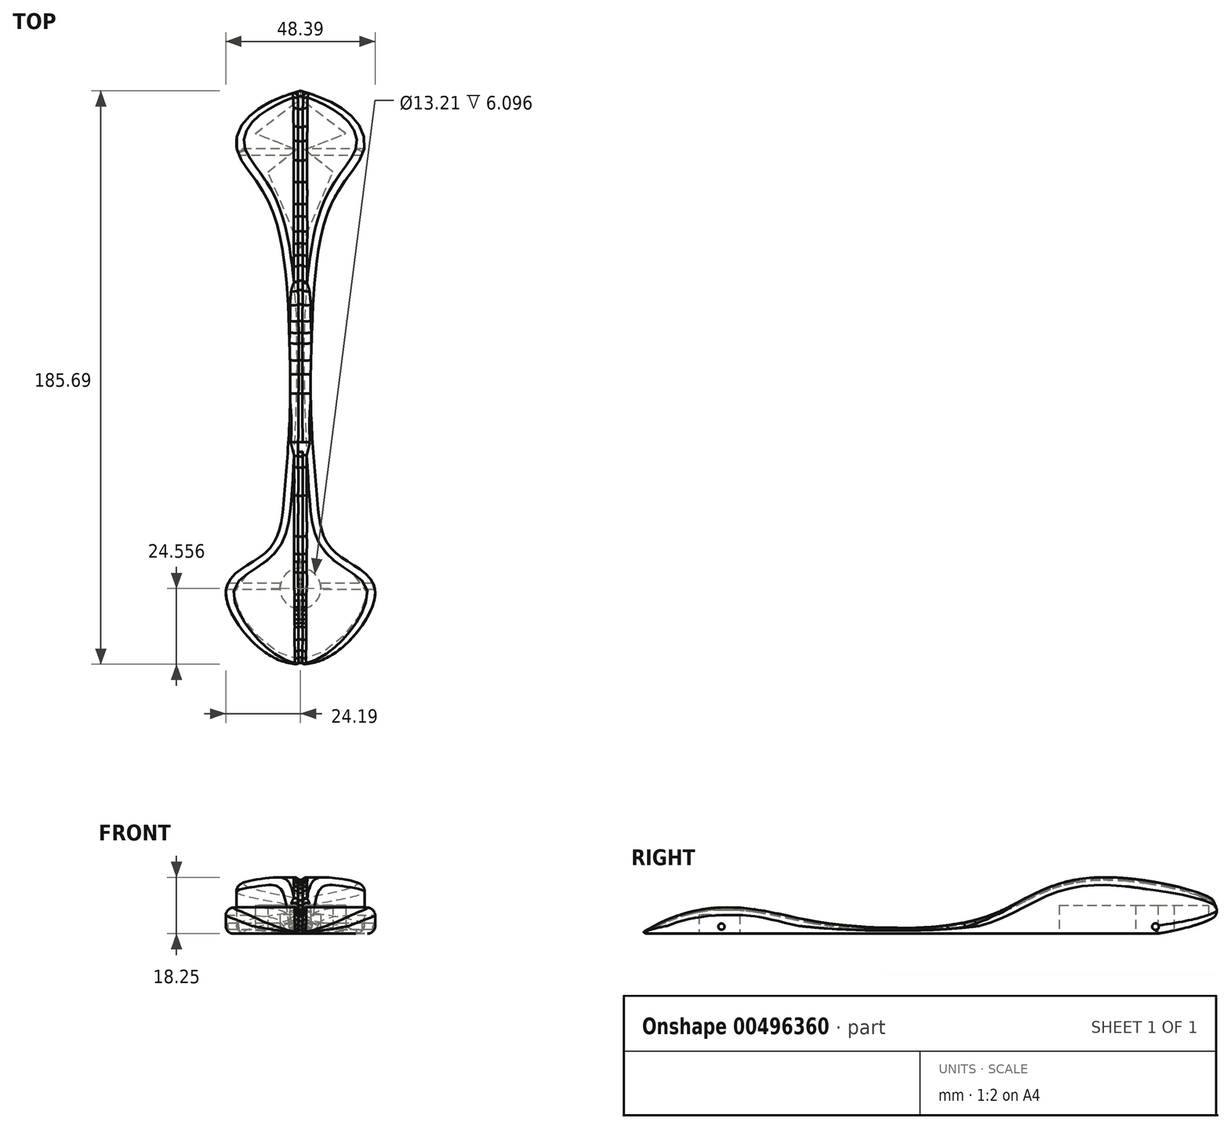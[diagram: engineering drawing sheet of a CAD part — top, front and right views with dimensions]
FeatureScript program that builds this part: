
annotation { "Feature Type Name" : "Feature", "Feature Type Description" : "" }
export const myFeature = defineFeature(function(context is Context, id is Id, definition is map)
    precondition{}
    {
        {
            var Q0;
            Q0=qCreatedBy(makeId("Right.planeOp"),FACE);
            var sketch = newSketch(context, id + "F0", { "sketchPlane" : qUnion([Q0])});
            skLineSegment(sketch, "E0", {"start": v(-99.64, 0) * mm, "end": v(67.86, 0) * mm});
            skFitSpline(sketch, "E1", {"points": [v(-99.64, 0) * mm, v(-58.26, 7.1) * mm, v(-36.9, 3.05) * mm, v(13.17, 6.08) * mm, v(63.97, 17.2) * mm, v(67.86, 0) * mm], "startDerivative": vector(226.28, 146.37) * mm, "endDerivative": vector(-818.18, -147.8) * mm});
            skCircle(sketch, "E2", {"center": v(-73.57, 2.29) * mm, "radius": 1.02 * mm});
            skCircle(sketch, "E3", {"center": v(67.09, 2.29) * mm, "radius": 1.08 * mm});
            skSolve(sketch);
        }
        {
            var Q0;
            Q0=makeQuery(id+"F0.imprint","IMPRINT",FACE,{"disambiguationData":[TD([[makeQuery(id+"F0.imprint","IMPRINT",EDGE,{"derivedFrom":sQuery(id+"F0.wireOp",EDGE,"E0")}),1.0]])]});
            extrude(context, id + "F1", {"entities" : qUnion([Q0]), "depth" : 81.28 * mm, "symmetric" : true});
        }
        {
            var Q0;
            Q0=qCreatedBy(makeId("Top.planeOp"),FACE);
            var sketch = newSketch(context, id + "F2", { "sketchPlane" : qUnion([Q0])});
            skFitSpline(sketch, "E4", {"points": [v(0.02, 86.91) * mm, v(-20.51, 67.7) * mm, v(-8.81, 47.48) * mm, v(-5.03, -39.8) * mm, v(-11.33, -62.63) * mm, v(-24.17, -75.03) * mm, v(0, -99.95) * mm], "startDerivative": vector(-340.64, -92.8) * mm, "endDerivative": vector(192.17, -7.55) * mm});
            skLineSegment(sketch, "E5", {"start": v(0.02, 86.91) * mm, "end": v(0.02, 86.91) * mm});
            skLineSegment(sketch, "E6.bottom", {"start": v(-52.6, 103.82) * mm, "end": v(52.64, 103.82) * mm});
            skLineSegment(sketch, "E6.top", {"start": v(-52.6, -103.34) * mm, "end": v(52.64, -103.34) * mm});
            skLineSegment(sketch, "E6.left", {"start": v(-52.6, 103.82) * mm, "end": v(-52.6, -103.34) * mm});
            skLineSegment(sketch, "E6.right", {"start": v(52.64, 103.82) * mm, "end": v(52.64, -103.34) * mm});
            skPoint(sketch, "E7.endSnap0", {"position": v(0.02, -103.34) * mm});
            skFitSpline(sketch, "E8.MirrorCS", {"points": [v(0.02, 86.91) * mm, v(20.55, 67.7) * mm, v(8.85, 47.48) * mm, v(5.05, -39.8) * mm, v(11.34, -62.63) * mm, v(24.17, -75.04) * mm, v(0, -99.95) * mm], "startDerivative": vector(340.62, -92.88) * mm, "endDerivative": vector(-192.17, -7.51) * mm});
            skSolve(sketch);
        }
        {
            var Q0;
            Q0=makeQuery(id+"F2.imprint","IMPRINT",FACE,{"disambiguationData":[TD([[makeQuery(id+"F2.imprint","IMPRINT",EDGE,{"derivedFrom":sQuery(id+"F2.wireOp",EDGE,"E6.top")}),1.0]])]});
            var Q1;
            Q1=qNothing();
            var Q2;
            Q2=qNothing();
            extrude(context, id + "F3", {"entities" : qUnion([Q0, Q1, Q2]), "operationType" : NewBodyOperationType.REMOVE, "oppositeDirection" : true, "depth" : 71.37 * mm, "offsetDistance" : 25.4 * mm, "symmetric" : true});
        }
        {
            var Q0;
            Q0=makeQuery(id+"F3.boolean.opBoolean","INTERSECT",EDGE,{"disambiguationData":[OD(1.0)],"derivedFrom":[makeQuery(id+"F1.opExtrude","SWEPT_FACE",FACE,{"disambiguationData":[OSD([sQuery(id+"F0.wireOp",EDGE,"E1")])]}),makeQuery(id+"F3.opExtrude","SWEPT_FACE",FACE,{"disambiguationData":[OSD([sQuery(id+"F2.wireOp",EDGE,"E8.MirrorCS")])]})]});
            var Q1;
            Q1=makeQuery(id+"F3.boolean.opBoolean","INTERSECT",EDGE,{"derivedFrom":[makeQuery(id+"F1.opExtrude","SWEPT_FACE",FACE,{"disambiguationData":[OSD([sQuery(id+"F0.wireOp",EDGE,"E0")])]}),makeQuery(id+"F3.opExtrude","SWEPT_FACE",FACE,{"disambiguationData":[OSD([sQuery(id+"F2.wireOp",EDGE,"E8.MirrorCS")])]})]});
            var Q2;
            Q2=makeQuery(id+"F3.boolean.opBoolean","INTERSECT",EDGE,{"derivedFrom":[makeQuery(id+"F1.opExtrude","SWEPT_FACE",FACE,{"disambiguationData":[OSD([sQuery(id+"F0.wireOp",EDGE,"E0")])]}),makeQuery(id+"F3.opExtrude","SWEPT_FACE",FACE,{"disambiguationData":[OSD([sQuery(id+"F2.wireOp",EDGE,"E4")])]})]});
            var Q3;
            Q3=makeQuery(id+"F3.boolean.opBoolean","INTERSECT",EDGE,{"disambiguationData":[OD(1.0)],"derivedFrom":[makeQuery(id+"F1.opExtrude","SWEPT_FACE",FACE,{"disambiguationData":[OSD([sQuery(id+"F0.wireOp",EDGE,"E1")])]}),makeQuery(id+"F3.opExtrude","SWEPT_FACE",FACE,{"disambiguationData":[OSD([sQuery(id+"F2.wireOp",EDGE,"E4")])]})]});
            var Q4;
            Q4=makeQuery(id+"F3.boolean.opBoolean","INTERSECT",EDGE,{"disambiguationData":[OD(0.0)],"derivedFrom":[makeQuery(id+"F1.opExtrude","SWEPT_FACE",FACE,{"disambiguationData":[OSD([sQuery(id+"F0.wireOp",EDGE,"E1")])]}),makeQuery(id+"F3.opExtrude","SWEPT_FACE",FACE,{"disambiguationData":[OSD([sQuery(id+"F2.wireOp",EDGE,"E4")])]})]});
            var Q5;
            Q5=makeQuery(id+"F3.boolean.opBoolean","INTERSECT",EDGE,{"disambiguationData":[OD(0.0)],"derivedFrom":[makeQuery(id+"F1.opExtrude","SWEPT_FACE",FACE,{"disambiguationData":[OSD([sQuery(id+"F0.wireOp",EDGE,"E1")])]}),makeQuery(id+"F3.opExtrude","SWEPT_FACE",FACE,{"disambiguationData":[OSD([sQuery(id+"F2.wireOp",EDGE,"E8.MirrorCS")])]})]});
            fillet(context, id + "F4", {"entities" : qUnion([Q0, Q1, Q2, Q3, Q4, Q5]), "radius" : 2.5 * mm, "tangentPropagation" : true, "allowEdgeOverflow" : false});
        }
        {
            var Q0;
            {var subQ0=sQuery(id+"F0.wireOp",EDGE,"E1");var subQ1=sQuery(id+"F0.wireOp",EDGE,"E0");Q0=makeQuery(id+"F1.opExtrude","SWEPT_EDGE",EDGE,{"disambiguationData":[OSD([subQ1,subQ0]),TDD([makeQuery(id+"F0.imprint","INTERSECT",VERTEX,{"disambiguationData":[OD(1.0)],"derivedFrom":[subQ1,subQ0]})])]});}
            fillet(context, id + "F5", {"entities" : qUnion([Q0]), "radius" : 2.5 * mm, "tangentPropagation" : true, "allowEdgeOverflow" : false});
        }
        {
            var Q0;
            Q0=qCreatedBy(makeId("Right.planeOp"),FACE);
            var sketch = newSketch(context, id + "F6", { "sketchPlane" : qUnion([Q0])});
            skLineSegment(sketch, "E9", {"start": v(-100.12, -0.3) * mm, "end": v(-96.89, 1.73) * mm});
            skLineSegment(sketch, "E10", {"start": v(-96.89, 1.73) * mm, "end": v(-94.53, 3) * mm});
            skLineSegment(sketch, "E11", {"start": v(-94.53, 3) * mm, "end": v(-90.9, 4.62) * mm});
            skLineSegment(sketch, "E12", {"start": v(-90.9, 4.62) * mm, "end": v(-86.85, 6.14) * mm});
            skLineSegment(sketch, "E13", {"start": v(-86.85, 6.14) * mm, "end": v(-85.54, 6.53) * mm});
            skLineSegment(sketch, "E14", {"start": v(-85.54, 6.53) * mm, "end": v(-84.06, 6.9) * mm});
            skLineSegment(sketch, "E15", {"start": v(-84.06, 6.9) * mm, "end": v(-82.72, 7.27) * mm});
            skLineSegment(sketch, "E16", {"start": v(-82.72, 7.27) * mm, "end": v(-81.34, 7.55) * mm});
            skLineSegment(sketch, "E17", {"start": v(-81.34, 7.55) * mm, "end": v(-80.05, 7.77) * mm});
            skLineSegment(sketch, "E18", {"start": v(-80.05, 7.77) * mm, "end": v(-78.2, 8.05) * mm});
            skLineSegment(sketch, "E19", {"start": v(-78.2, 8.05) * mm, "end": v(-76.17, 8.31) * mm});
            skLineSegment(sketch, "E20", {"start": v(-76.17, 8.31) * mm, "end": v(-75.14, 8.31) * mm});
            skLineSegment(sketch, "E21", {"start": v(-75.14, 8.31) * mm, "end": v(-74.38, 8.31) * mm});
            skLineSegment(sketch, "E22", {"start": v(-74.38, 8.31) * mm, "end": v(-73.62, 8.31) * mm});
            skLineSegment(sketch, "E23", {"start": v(-73.62, 8.31) * mm, "end": v(-72.47, 8.31) * mm});
            skLineSegment(sketch, "E24", {"start": v(-72.47, 8.31) * mm, "end": v(-70.97, 8.31) * mm});
            skLineSegment(sketch, "E25", {"start": v(-70.97, 8.31) * mm, "end": v(-69.08, 8.31) * mm});
            skLineSegment(sketch, "E26", {"start": v(-69.08, 8.31) * mm, "end": v(-65.6, 8.05) * mm});
            skLineSegment(sketch, "E27", {"start": v(-65.6, 8.05) * mm, "end": v(-63.1, 7.77) * mm});
            skLineSegment(sketch, "E28", {"start": v(-63.1, 7.77) * mm, "end": v(-61.86, 7.55) * mm});
            skLineSegment(sketch, "E29", {"start": v(-61.86, 7.55) * mm, "end": v(-57.31, 6.74) * mm});
            skLineSegment(sketch, "E30", {"start": v(-57.31, 6.74) * mm, "end": v(-50.98, 5.38) * mm});
            skLineSegment(sketch, "E31", {"start": v(-50.98, 5.38) * mm, "end": v(-44.16, 3.93) * mm});
            skLineSegment(sketch, "E32", {"start": v(-44.16, 3.93) * mm, "end": v(-39.73, 3.3) * mm});
            skLineSegment(sketch, "E33", {"start": v(-39.73, 3.3) * mm, "end": v(-35.03, 2.65) * mm});
            skLineSegment(sketch, "E34", {"start": v(-35.03, 2.65) * mm, "end": v(-31.08, 2.3) * mm});
            skLineSegment(sketch, "E35", {"start": v(-31.08, 2.3) * mm, "end": v(-29.62, 2.18) * mm});
            skLineSegment(sketch, "E36", {"start": v(-29.62, 2.18) * mm, "end": v(-26.88, 1.95) * mm});
            skLineSegment(sketch, "E37", {"start": v(-26.88, 1.95) * mm, "end": v(-11.11, 1.95) * mm});
            skLineSegment(sketch, "E38", {"start": v(-11.11, 1.95) * mm, "end": v(-4.94, 2.3) * mm});
            skLineSegment(sketch, "E39", {"start": v(-4.94, 2.3) * mm, "end": v(-0.44, 2.85) * mm});
            skLineSegment(sketch, "E40", {"start": v(-0.44, 2.85) * mm, "end": v(5.05, 3.71) * mm});
            skLineSegment(sketch, "E41", {"start": v(5.05, 3.71) * mm, "end": v(8.48, 4.5) * mm});
            skLineSegment(sketch, "E42", {"start": v(8.48, 4.5) * mm, "end": v(12.27, 5.6) * mm});
            skLineSegment(sketch, "E43", {"start": v(12.27, 5.6) * mm, "end": v(17.56, 7.55) * mm});
            skLineSegment(sketch, "E44", {"start": v(17.56, 7.55) * mm, "end": v(22.11, 9.75) * mm});
            skLineSegment(sketch, "E45", {"start": v(22.11, 9.75) * mm, "end": v(25.16, 11.37) * mm});
            skLineSegment(sketch, "E46", {"start": v(25.16, 11.37) * mm, "end": v(30.14, 13.72) * mm});
            skLineSegment(sketch, "E47", {"start": v(30.14, 13.72) * mm, "end": v(33.58, 15.2) * mm});
            skLineSegment(sketch, "E48", {"start": v(33.58, 15.2) * mm, "end": v(37.43, 16.39) * mm});
            skLineSegment(sketch, "E49", {"start": v(37.43, 16.39) * mm, "end": v(41.38, 17.17) * mm});
            skLineSegment(sketch, "E50", {"start": v(41.38, 17.17) * mm, "end": v(46.2, 17.83) * mm});
            skLineSegment(sketch, "E51", {"start": v(46.2, 17.83) * mm, "end": v(50.27, 18.01) * mm});
            skLineSegment(sketch, "E52", {"start": v(50.27, 18.01) * mm, "end": v(57.35, 17.73) * mm});
            skLineSegment(sketch, "E53", {"start": v(57.35, 17.73) * mm, "end": v(64.38, 16.89) * mm});
            skLineSegment(sketch, "E54", {"start": v(64.38, 16.89) * mm, "end": v(70.72, 15.74) * mm});
            skLineSegment(sketch, "E55", {"start": v(70.72, 15.74) * mm, "end": v(75.31, 14.6) * mm});
            skLineSegment(sketch, "E56", {"start": v(75.31, 14.6) * mm, "end": v(81.23, 12.8) * mm});
            skLineSegment(sketch, "E57", {"start": v(81.23, 12.8) * mm, "end": v(85.48, 10.83) * mm});
            skLineSegment(sketch, "E58", {"start": v(85.48, 10.83) * mm, "end": v(90.33, 4.3) * mm});
            skSolve(sketch);
        }
        {
            var Q0;
            Q0=qCreatedBy(makeId("Front.planeOp"),FACE);
            var Q1;
            Q1=sQuery(id+"F6.wireOp",VERTEX,"E9.start");
            cPlane(context, id + "F7", {"entities" : qUnion([Q0, Q1]), "cplaneType" : CPlaneType.PLANE_POINT, "offset" : 91.95 * mm, "width" : 152.4 * mm, "height" : 152.4 * mm});
        }
        {
            var Q0;
            Q0=qCreatedBy(id+"F7.planeOp",FACE);
            var sketch = newSketch(context, id + "F8", { "sketchPlane" : qUnion([Q0])});
            skCircle(sketch, "E59", {"center": v(0, 0) * mm, "radius": 1 * mm});
            skSolve(sketch);
        }
        {
            var Q0;
            Q0=makeQuery(id+"F8.imprint","IMPRINT",FACE,{"disambiguationData":[TD([[makeQuery(id+"F8.imprint","IMPRINT",EDGE,{"derivedFrom":sQuery(id+"F8.wireOp",EDGE,"E59")}),1.0]])]});
            var Q1;
            Q1=sQuery(id+"F6.wireOp",EDGE,"E9");
            var Q2;
            Q2=sQuery(id+"F6.wireOp",EDGE,"E10");
            var Q3;
            Q3=sQuery(id+"F6.wireOp",EDGE,"E37");
            var Q4;
            Q4=sQuery(id+"F6.wireOp",EDGE,"E58");
            var Q5;
            Q5=sQuery(id+"F6.wireOp",EDGE,"E11");
            var Q6;
            Q6=sQuery(id+"F6.wireOp",EDGE,"E12");
            var Q7;
            Q7=sQuery(id+"F6.wireOp",EDGE,"E18");
            var Q8;
            Q8=sQuery(id+"F6.wireOp",EDGE,"E49");
            var Q9;
            Q9=sQuery(id+"F6.wireOp",EDGE,"E43");
            var Q10;
            Q10=sQuery(id+"F6.wireOp",EDGE,"E27");
            var Q11;
            Q11=sQuery(id+"F6.wireOp",EDGE,"E50");
            var Q12;
            Q12=sQuery(id+"F6.wireOp",EDGE,"E34");
            var Q13;
            Q13=sQuery(id+"F6.wireOp",EDGE,"E51");
            var Q14;
            Q14=sQuery(id+"F6.wireOp",EDGE,"E44");
            var Q15;
            Q15=sQuery(id+"F6.wireOp",EDGE,"E28");
            var Q16;
            Q16=sQuery(id+"F6.wireOp",EDGE,"E52");
            var Q17;
            Q17=sQuery(id+"F6.wireOp",EDGE,"E36");
            var Q18;
            Q18=sQuery(id+"F6.wireOp",EDGE,"E54");
            var Q19;
            Q19=sQuery(id+"F6.wireOp",EDGE,"E45");
            var Q20;
            Q20=sQuery(id+"F6.wireOp",EDGE,"E38");
            var Q21;
            Q21=sQuery(id+"F6.wireOp",EDGE,"E29");
            var Q22;
            Q22=sQuery(id+"F6.wireOp",EDGE,"E53");
            var Q23;
            Q23=sQuery(id+"F6.wireOp",EDGE,"E55");
            var Q24;
            Q24=sQuery(id+"F6.wireOp",EDGE,"E39");
            var Q25;
            Q25=sQuery(id+"F6.wireOp",EDGE,"E46");
            var Q26;
            Q26=sQuery(id+"F6.wireOp",EDGE,"E30");
            var Q27;
            Q27=sQuery(id+"F6.wireOp",EDGE,"E56");
            var Q28;
            Q28=sQuery(id+"F6.wireOp",EDGE,"E40");
            var Q29;
            Q29=sQuery(id+"F6.wireOp",EDGE,"E47");
            var Q30;
            Q30=sQuery(id+"F6.wireOp",EDGE,"E31");
            var Q31;
            Q31=sQuery(id+"F6.wireOp",EDGE,"E57");
            var Q32;
            Q32=sQuery(id+"F6.wireOp",EDGE,"E41");
            var Q33;
            Q33=sQuery(id+"F6.wireOp",EDGE,"E48");
            var Q34;
            Q34=sQuery(id+"F6.wireOp",EDGE,"E32");
            var Q35;
            Q35=sQuery(id+"F6.wireOp",EDGE,"E42");
            var Q36;
            Q36=sQuery(id+"F6.wireOp",EDGE,"E26");
            var Q37;
            Q37=sQuery(id+"F6.wireOp",EDGE,"E17");
            var Q38;
            Q38=sQuery(id+"F6.wireOp",EDGE,"E33");
            var Q39;
            Q39=sQuery(id+"F6.wireOp",EDGE,"E35");
            var Q40;
            Q40=sQuery(id+"F6.wireOp",EDGE,"E13");
            var Q41;
            Q41=sQuery(id+"F6.wireOp",EDGE,"E16");
            var Q42;
            Q42=sQuery(id+"F6.wireOp",EDGE,"E15");
            var Q43;
            Q43=sQuery(id+"F6.wireOp",EDGE,"E14");
            var Q44;
            Q44=sQuery(id+"F6.wireOp",EDGE,"E23");
            var Q45;
            Q45=sQuery(id+"F6.wireOp",EDGE,"E19");
            var Q46;
            Q46=sQuery(id+"F6.wireOp",EDGE,"E21");
            var Q47;
            Q47=sQuery(id+"F6.wireOp",EDGE,"E25");
            var Q48;
            Q48=sQuery(id+"F6.wireOp",EDGE,"E22");
            var Q49;
            Q49=sQuery(id+"F6.wireOp",EDGE,"E24");
            var Q50;
            Q50=sQuery(id+"F6.wireOp",EDGE,"E20");
            sweep(context, id + "F9", {"operationType" : NewBodyOperationType.REMOVE, "profiles" : qUnion([Q0]), "path" : qUnion([Q1, Q2, Q3, Q4, Q5, Q6, Q7, Q8, Q9, Q10, Q11, Q12, Q13, Q14, Q15, Q16, Q17, Q18, Q19, Q20, Q21, Q22, Q23, Q24, Q25, Q26, Q27, Q28, Q29, Q30, Q31, Q32, Q33, Q34, Q35, Q36, Q37, Q38, Q39, Q40, Q41, Q42, Q43, Q44, Q45, Q46, Q47, Q48, Q49, Q50])});
        }
        {
            var Q0;
            Q0=makeQuery(id+"F9.boolean.opBoolean","INTERSECT",EDGE,{"disambiguationData":[OD(1.0)],"derivedFrom":[makeQuery(id+"F3.boolean.opBoolean","SPLIT",FACE,{"disambiguationData":[OD(0.0)],"derivedFrom":makeQuery(id+"F1.opExtrude","SWEPT_FACE",FACE,{"disambiguationData":[OSD([sQuery(id+"F0.wireOp",EDGE,"E1")])]})}),makeQuery(id+"F9.opSweep","SWEPT_FACE",FACE,{"disambiguationData":[OSD([sQuery(id+"F6.wireOp",EDGE,"E9"),sQuery(id+"F8.wireOp",EDGE,"E59")])]})]});
            var Q1;
            Q1=makeQuery(id+"F9.boolean.opBoolean","INTERSECT",EDGE,{"disambiguationData":[OD(1.0)],"derivedFrom":[makeQuery(id+"F3.boolean.opBoolean","SPLIT",FACE,{"disambiguationData":[OD(0.0)],"derivedFrom":makeQuery(id+"F1.opExtrude","SWEPT_FACE",FACE,{"disambiguationData":[OSD([sQuery(id+"F0.wireOp",EDGE,"E1")])]})}),makeQuery(id+"F9.opSweep","SWEPT_FACE",FACE,{"disambiguationData":[OSD([sQuery(id+"F6.wireOp",EDGE,"E10"),sQuery(id+"F8.wireOp",EDGE,"E59")])]})]});
            var Q2;
            Q2=makeQuery(id+"F9.boolean.opBoolean","INTERSECT",EDGE,{"disambiguationData":[OD(1.0)],"derivedFrom":[makeQuery(id+"F3.boolean.opBoolean","SPLIT",FACE,{"disambiguationData":[OD(0.0)],"derivedFrom":makeQuery(id+"F1.opExtrude","SWEPT_FACE",FACE,{"disambiguationData":[OSD([sQuery(id+"F0.wireOp",EDGE,"E1")])]})}),makeQuery(id+"F9.opSweep","SWEPT_FACE",FACE,{"disambiguationData":[OSD([sQuery(id+"F6.wireOp",EDGE,"E11"),sQuery(id+"F8.wireOp",EDGE,"E59")])]})]});
            var Q3;
            Q3=makeQuery(id+"F9.boolean.opBoolean","INTERSECT",EDGE,{"disambiguationData":[OD(1.0)],"derivedFrom":[makeQuery(id+"F3.boolean.opBoolean","SPLIT",FACE,{"disambiguationData":[OD(0.0)],"derivedFrom":makeQuery(id+"F1.opExtrude","SWEPT_FACE",FACE,{"disambiguationData":[OSD([sQuery(id+"F0.wireOp",EDGE,"E1")])]})}),makeQuery(id+"F9.opSweep","SWEPT_FACE",FACE,{"disambiguationData":[OSD([sQuery(id+"F6.wireOp",EDGE,"E12"),sQuery(id+"F8.wireOp",EDGE,"E59")])]})]});
            var Q4;
            Q4=makeQuery(id+"F9.boolean.opBoolean","INTERSECT",EDGE,{"disambiguationData":[OD(1.0)],"derivedFrom":[makeQuery(id+"F3.boolean.opBoolean","SPLIT",FACE,{"disambiguationData":[OD(0.0)],"derivedFrom":makeQuery(id+"F1.opExtrude","SWEPT_FACE",FACE,{"disambiguationData":[OSD([sQuery(id+"F0.wireOp",EDGE,"E1")])]})}),makeQuery(id+"F9.opSweep","SWEPT_FACE",FACE,{"disambiguationData":[OSD([sQuery(id+"F6.wireOp",EDGE,"E13"),sQuery(id+"F8.wireOp",EDGE,"E59")])]})]});
            var Q5;
            Q5=makeQuery(id+"F9.boolean.opBoolean","INTERSECT",EDGE,{"disambiguationData":[OD(1.0)],"derivedFrom":[makeQuery(id+"F3.boolean.opBoolean","SPLIT",FACE,{"disambiguationData":[OD(0.0)],"derivedFrom":makeQuery(id+"F1.opExtrude","SWEPT_FACE",FACE,{"disambiguationData":[OSD([sQuery(id+"F0.wireOp",EDGE,"E1")])]})}),makeQuery(id+"F9.opSweep","SWEPT_FACE",FACE,{"disambiguationData":[OSD([sQuery(id+"F6.wireOp",EDGE,"E14"),sQuery(id+"F8.wireOp",EDGE,"E59")])]})]});
            var Q6;
            Q6=makeQuery(id+"F9.boolean.opBoolean","INTERSECT",EDGE,{"disambiguationData":[OD(1.0)],"derivedFrom":[makeQuery(id+"F3.boolean.opBoolean","SPLIT",FACE,{"disambiguationData":[OD(0.0)],"derivedFrom":makeQuery(id+"F1.opExtrude","SWEPT_FACE",FACE,{"disambiguationData":[OSD([sQuery(id+"F0.wireOp",EDGE,"E1")])]})}),makeQuery(id+"F9.opSweep","SWEPT_FACE",FACE,{"disambiguationData":[OSD([sQuery(id+"F6.wireOp",EDGE,"E15"),sQuery(id+"F8.wireOp",EDGE,"E59")])]})]});
            var Q7;
            Q7=makeQuery(id+"F9.boolean.opBoolean","INTERSECT",EDGE,{"disambiguationData":[OD(1.0)],"derivedFrom":[makeQuery(id+"F3.boolean.opBoolean","SPLIT",FACE,{"disambiguationData":[OD(0.0)],"derivedFrom":makeQuery(id+"F1.opExtrude","SWEPT_FACE",FACE,{"disambiguationData":[OSD([sQuery(id+"F0.wireOp",EDGE,"E1")])]})}),makeQuery(id+"F9.opSweep","SWEPT_FACE",FACE,{"disambiguationData":[OSD([sQuery(id+"F6.wireOp",EDGE,"E16"),sQuery(id+"F8.wireOp",EDGE,"E59")])]})]});
            var Q8;
            Q8=makeQuery(id+"F9.boolean.opBoolean","INTERSECT",EDGE,{"disambiguationData":[OD(1.0)],"derivedFrom":[makeQuery(id+"F3.boolean.opBoolean","SPLIT",FACE,{"disambiguationData":[OD(0.0)],"derivedFrom":makeQuery(id+"F1.opExtrude","SWEPT_FACE",FACE,{"disambiguationData":[OSD([sQuery(id+"F0.wireOp",EDGE,"E1")])]})}),makeQuery(id+"F9.opSweep","SWEPT_FACE",FACE,{"disambiguationData":[OSD([sQuery(id+"F6.wireOp",EDGE,"E17"),sQuery(id+"F8.wireOp",EDGE,"E59")])]})]});
            var Q9;
            Q9=makeQuery(id+"F9.boolean.opBoolean","INTERSECT",EDGE,{"disambiguationData":[OD(1.0)],"derivedFrom":[makeQuery(id+"F3.boolean.opBoolean","SPLIT",FACE,{"disambiguationData":[OD(0.0)],"derivedFrom":makeQuery(id+"F1.opExtrude","SWEPT_FACE",FACE,{"disambiguationData":[OSD([sQuery(id+"F0.wireOp",EDGE,"E1")])]})}),makeQuery(id+"F9.opSweep","SWEPT_FACE",FACE,{"disambiguationData":[OSD([sQuery(id+"F6.wireOp",EDGE,"E18"),sQuery(id+"F8.wireOp",EDGE,"E59")])]})]});
            var Q10;
            Q10=makeQuery(id+"F9.boolean.opBoolean","INTERSECT",EDGE,{"disambiguationData":[OD(1.0)],"derivedFrom":[makeQuery(id+"F3.boolean.opBoolean","SPLIT",FACE,{"disambiguationData":[OD(0.0)],"derivedFrom":makeQuery(id+"F1.opExtrude","SWEPT_FACE",FACE,{"disambiguationData":[OSD([sQuery(id+"F0.wireOp",EDGE,"E1")])]})}),makeQuery(id+"F9.opSweep","SWEPT_FACE",FACE,{"disambiguationData":[OSD([sQuery(id+"F6.wireOp",EDGE,"E19"),sQuery(id+"F8.wireOp",EDGE,"E59")])]})]});
            var Q11;
            Q11=makeQuery(id+"F9.boolean.opBoolean","INTERSECT",EDGE,{"disambiguationData":[OD(1.0)],"derivedFrom":[makeQuery(id+"F3.boolean.opBoolean","SPLIT",FACE,{"disambiguationData":[OD(0.0)],"derivedFrom":makeQuery(id+"F1.opExtrude","SWEPT_FACE",FACE,{"disambiguationData":[OSD([sQuery(id+"F0.wireOp",EDGE,"E1")])]})}),makeQuery(id+"F9.opSweep","SWEPT_FACE",FACE,{"disambiguationData":[OSD([sQuery(id+"F6.wireOp",EDGE,"E20"),sQuery(id+"F8.wireOp",EDGE,"E59")])]})]});
            var Q12;
            Q12=makeQuery(id+"F9.boolean.opBoolean","INTERSECT",EDGE,{"disambiguationData":[OD(1.0)],"derivedFrom":[makeQuery(id+"F3.boolean.opBoolean","SPLIT",FACE,{"disambiguationData":[OD(0.0)],"derivedFrom":makeQuery(id+"F1.opExtrude","SWEPT_FACE",FACE,{"disambiguationData":[OSD([sQuery(id+"F0.wireOp",EDGE,"E1")])]})}),makeQuery(id+"F9.opSweep","SWEPT_FACE",FACE,{"disambiguationData":[OSD([sQuery(id+"F6.wireOp",EDGE,"E21"),sQuery(id+"F8.wireOp",EDGE,"E59")])]})]});
            var Q13;
            Q13=makeQuery(id+"F9.boolean.opBoolean","INTERSECT",EDGE,{"disambiguationData":[OD(1.0)],"derivedFrom":[makeQuery(id+"F3.boolean.opBoolean","SPLIT",FACE,{"disambiguationData":[OD(0.0)],"derivedFrom":makeQuery(id+"F1.opExtrude","SWEPT_FACE",FACE,{"disambiguationData":[OSD([sQuery(id+"F0.wireOp",EDGE,"E1")])]})}),makeQuery(id+"F9.opSweep","SWEPT_FACE",FACE,{"disambiguationData":[OSD([sQuery(id+"F6.wireOp",EDGE,"E22"),sQuery(id+"F8.wireOp",EDGE,"E59")])]})]});
            var Q14;
            Q14=makeQuery(id+"F9.boolean.opBoolean","INTERSECT",EDGE,{"disambiguationData":[OD(1.0)],"derivedFrom":[makeQuery(id+"F3.boolean.opBoolean","SPLIT",FACE,{"disambiguationData":[OD(0.0)],"derivedFrom":makeQuery(id+"F1.opExtrude","SWEPT_FACE",FACE,{"disambiguationData":[OSD([sQuery(id+"F0.wireOp",EDGE,"E1")])]})}),makeQuery(id+"F9.opSweep","SWEPT_FACE",FACE,{"disambiguationData":[OSD([sQuery(id+"F6.wireOp",EDGE,"E23"),sQuery(id+"F8.wireOp",EDGE,"E59")])]})]});
            var Q15;
            Q15=makeQuery(id+"F9.boolean.opBoolean","INTERSECT",EDGE,{"disambiguationData":[OD(1.0)],"derivedFrom":[makeQuery(id+"F3.boolean.opBoolean","SPLIT",FACE,{"disambiguationData":[OD(0.0)],"derivedFrom":makeQuery(id+"F1.opExtrude","SWEPT_FACE",FACE,{"disambiguationData":[OSD([sQuery(id+"F0.wireOp",EDGE,"E1")])]})}),makeQuery(id+"F9.opSweep","SWEPT_FACE",FACE,{"disambiguationData":[OSD([sQuery(id+"F6.wireOp",EDGE,"E24"),sQuery(id+"F8.wireOp",EDGE,"E59")])]})]});
            var Q16;
            Q16=makeQuery(id+"F9.boolean.opBoolean","INTERSECT",EDGE,{"disambiguationData":[OD(1.0)],"derivedFrom":[makeQuery(id+"F3.boolean.opBoolean","SPLIT",FACE,{"disambiguationData":[OD(0.0)],"derivedFrom":makeQuery(id+"F1.opExtrude","SWEPT_FACE",FACE,{"disambiguationData":[OSD([sQuery(id+"F0.wireOp",EDGE,"E1")])]})}),makeQuery(id+"F9.opSweep","SWEPT_FACE",FACE,{"disambiguationData":[OSD([sQuery(id+"F6.wireOp",EDGE,"E25"),sQuery(id+"F8.wireOp",EDGE,"E59")])]})]});
            var Q17;
            Q17=makeQuery(id+"F9.boolean.opBoolean","INTERSECT",EDGE,{"disambiguationData":[OD(1.0)],"derivedFrom":[makeQuery(id+"F3.boolean.opBoolean","SPLIT",FACE,{"disambiguationData":[OD(0.0)],"derivedFrom":makeQuery(id+"F1.opExtrude","SWEPT_FACE",FACE,{"disambiguationData":[OSD([sQuery(id+"F0.wireOp",EDGE,"E1")])]})}),makeQuery(id+"F9.opSweep","SWEPT_FACE",FACE,{"disambiguationData":[OSD([sQuery(id+"F6.wireOp",EDGE,"E26"),sQuery(id+"F8.wireOp",EDGE,"E59")])]})]});
            var Q18;
            Q18=makeQuery(id+"F9.boolean.opBoolean","INTERSECT",EDGE,{"disambiguationData":[OD(1.0)],"derivedFrom":[makeQuery(id+"F3.boolean.opBoolean","SPLIT",FACE,{"disambiguationData":[OD(0.0)],"derivedFrom":makeQuery(id+"F1.opExtrude","SWEPT_FACE",FACE,{"disambiguationData":[OSD([sQuery(id+"F0.wireOp",EDGE,"E1")])]})}),makeQuery(id+"F9.opSweep","SWEPT_FACE",FACE,{"disambiguationData":[OSD([sQuery(id+"F6.wireOp",EDGE,"E27"),sQuery(id+"F8.wireOp",EDGE,"E59")])]})]});
            var Q19;
            Q19=makeQuery(id+"F9.boolean.opBoolean","INTERSECT",EDGE,{"disambiguationData":[OD(1.0)],"derivedFrom":[makeQuery(id+"F3.boolean.opBoolean","SPLIT",FACE,{"disambiguationData":[OD(0.0)],"derivedFrom":makeQuery(id+"F1.opExtrude","SWEPT_FACE",FACE,{"disambiguationData":[OSD([sQuery(id+"F0.wireOp",EDGE,"E1")])]})}),makeQuery(id+"F9.opSweep","SWEPT_FACE",FACE,{"disambiguationData":[OSD([sQuery(id+"F6.wireOp",EDGE,"E28"),sQuery(id+"F8.wireOp",EDGE,"E59")])]})]});
            var Q20;
            Q20=makeQuery(id+"F9.boolean.opBoolean","INTERSECT",EDGE,{"disambiguationData":[OD(1.0)],"derivedFrom":[makeQuery(id+"F3.boolean.opBoolean","SPLIT",FACE,{"disambiguationData":[OD(0.0)],"derivedFrom":makeQuery(id+"F1.opExtrude","SWEPT_FACE",FACE,{"disambiguationData":[OSD([sQuery(id+"F0.wireOp",EDGE,"E1")])]})}),makeQuery(id+"F9.opSweep","SWEPT_FACE",FACE,{"disambiguationData":[OSD([sQuery(id+"F6.wireOp",EDGE,"E29"),sQuery(id+"F8.wireOp",EDGE,"E59")])]})]});
            var Q21;
            Q21=makeQuery(id+"F9.boolean.opBoolean","INTERSECT",EDGE,{"disambiguationData":[OD(1.0)],"derivedFrom":[makeQuery(id+"F3.boolean.opBoolean","SPLIT",FACE,{"disambiguationData":[OD(0.0)],"derivedFrom":makeQuery(id+"F1.opExtrude","SWEPT_FACE",FACE,{"disambiguationData":[OSD([sQuery(id+"F0.wireOp",EDGE,"E1")])]})}),makeQuery(id+"F9.opSweep","SWEPT_FACE",FACE,{"disambiguationData":[OSD([sQuery(id+"F6.wireOp",EDGE,"E30"),sQuery(id+"F8.wireOp",EDGE,"E59")])]})]});
            var Q22;
            Q22=makeQuery(id+"F9.boolean.opBoolean","INTERSECT",EDGE,{"disambiguationData":[OD(1.0)],"derivedFrom":[makeQuery(id+"F3.boolean.opBoolean","SPLIT",FACE,{"disambiguationData":[OD(0.0)],"derivedFrom":makeQuery(id+"F1.opExtrude","SWEPT_FACE",FACE,{"disambiguationData":[OSD([sQuery(id+"F0.wireOp",EDGE,"E1")])]})}),makeQuery(id+"F9.opSweep","SWEPT_FACE",FACE,{"disambiguationData":[OSD([sQuery(id+"F6.wireOp",EDGE,"E31"),sQuery(id+"F8.wireOp",EDGE,"E59")])]})]});
            var Q23;
            Q23=makeQuery(id+"F9.boolean.opBoolean","INTERSECT",EDGE,{"disambiguationData":[OD(1.0)],"derivedFrom":[makeQuery(id+"F3.boolean.opBoolean","SPLIT",FACE,{"disambiguationData":[OD(0.0)],"derivedFrom":makeQuery(id+"F1.opExtrude","SWEPT_FACE",FACE,{"disambiguationData":[OSD([sQuery(id+"F0.wireOp",EDGE,"E1")])]})}),makeQuery(id+"F9.opSweep","SWEPT_FACE",FACE,{"disambiguationData":[OSD([sQuery(id+"F6.wireOp",EDGE,"E32"),sQuery(id+"F8.wireOp",EDGE,"E59")])]})]});
            var Q24;
            Q24=makeQuery(id+"F9.boolean.opBoolean","INTERSECT",EDGE,{"disambiguationData":[OD(1.0)],"derivedFrom":[makeQuery(id+"F3.boolean.opBoolean","SPLIT",FACE,{"disambiguationData":[OD(0.0)],"derivedFrom":makeQuery(id+"F1.opExtrude","SWEPT_FACE",FACE,{"disambiguationData":[OSD([sQuery(id+"F0.wireOp",EDGE,"E1")])]})}),makeQuery(id+"F9.opSweep","SWEPT_FACE",FACE,{"disambiguationData":[OSD([sQuery(id+"F6.wireOp",EDGE,"E33"),sQuery(id+"F8.wireOp",EDGE,"E59")])]})]});
            var Q25;
            Q25=makeQuery(id+"F9.boolean.opBoolean","INTERSECT",EDGE,{"disambiguationData":[OD(1.0)],"derivedFrom":[makeQuery(id+"F3.boolean.opBoolean","SPLIT",FACE,{"disambiguationData":[OD(0.0)],"derivedFrom":makeQuery(id+"F1.opExtrude","SWEPT_FACE",FACE,{"disambiguationData":[OSD([sQuery(id+"F0.wireOp",EDGE,"E1")])]})}),makeQuery(id+"F9.opSweep","SWEPT_FACE",FACE,{"disambiguationData":[OSD([sQuery(id+"F6.wireOp",EDGE,"E34"),sQuery(id+"F8.wireOp",EDGE,"E59")])]})]});
            var Q26;
            Q26=makeQuery(id+"F9.boolean.opBoolean","INTERSECT",EDGE,{"disambiguationData":[OD(1.0)],"derivedFrom":[makeQuery(id+"F3.boolean.opBoolean","SPLIT",FACE,{"disambiguationData":[OD(0.0)],"derivedFrom":makeQuery(id+"F1.opExtrude","SWEPT_FACE",FACE,{"disambiguationData":[OSD([sQuery(id+"F0.wireOp",EDGE,"E1")])]})}),makeQuery(id+"F9.opSweep","SWEPT_FACE",FACE,{"disambiguationData":[OSD([sQuery(id+"F6.wireOp",EDGE,"E35"),sQuery(id+"F8.wireOp",EDGE,"E59")])]})]});
            var Q27;
            Q27=makeQuery(id+"F9.boolean.opBoolean","INTERSECT",EDGE,{"disambiguationData":[OD(1.0)],"derivedFrom":[makeQuery(id+"F3.boolean.opBoolean","SPLIT",FACE,{"disambiguationData":[OD(0.0)],"derivedFrom":makeQuery(id+"F1.opExtrude","SWEPT_FACE",FACE,{"disambiguationData":[OSD([sQuery(id+"F0.wireOp",EDGE,"E1")])]})}),makeQuery(id+"F9.opSweep","SWEPT_FACE",FACE,{"disambiguationData":[OSD([sQuery(id+"F6.wireOp",EDGE,"E36"),sQuery(id+"F8.wireOp",EDGE,"E59")])]})]});
            var Q28;
            Q28=makeQuery(id+"F9.boolean.opBoolean","INTERSECT",EDGE,{"disambiguationData":[OD(1.0)],"derivedFrom":[makeQuery(id+"F3.boolean.opBoolean","SPLIT",FACE,{"disambiguationData":[OD(0.0)],"derivedFrom":makeQuery(id+"F1.opExtrude","SWEPT_FACE",FACE,{"disambiguationData":[OSD([sQuery(id+"F0.wireOp",EDGE,"E1")])]})}),makeQuery(id+"F9.opSweep","SWEPT_FACE",FACE,{"disambiguationData":[OSD([sQuery(id+"F6.wireOp",EDGE,"E37"),sQuery(id+"F8.wireOp",EDGE,"E59")])]})]});
            var Q29;
            Q29=makeQuery(id+"F9.boolean.opBoolean","INTERSECT",EDGE,{"disambiguationData":[OD(1.0)],"derivedFrom":[makeQuery(id+"F3.boolean.opBoolean","SPLIT",FACE,{"disambiguationData":[OD(0.0)],"derivedFrom":makeQuery(id+"F1.opExtrude","SWEPT_FACE",FACE,{"disambiguationData":[OSD([sQuery(id+"F0.wireOp",EDGE,"E1")])]})}),makeQuery(id+"F9.opSweep","SWEPT_FACE",FACE,{"disambiguationData":[OSD([sQuery(id+"F6.wireOp",EDGE,"E38"),sQuery(id+"F8.wireOp",EDGE,"E59")])]})]});
            var Q30;
            Q30=makeQuery(id+"F9.boolean.opBoolean","INTERSECT",EDGE,{"disambiguationData":[OD(1.0)],"derivedFrom":[makeQuery(id+"F3.boolean.opBoolean","SPLIT",FACE,{"disambiguationData":[OD(0.0)],"derivedFrom":makeQuery(id+"F1.opExtrude","SWEPT_FACE",FACE,{"disambiguationData":[OSD([sQuery(id+"F0.wireOp",EDGE,"E1")])]})}),makeQuery(id+"F9.opSweep","SWEPT_FACE",FACE,{"disambiguationData":[OSD([sQuery(id+"F6.wireOp",EDGE,"E39"),sQuery(id+"F8.wireOp",EDGE,"E59")])]})]});
            var Q31;
            Q31=makeQuery(id+"F9.boolean.opBoolean","INTERSECT",EDGE,{"disambiguationData":[OD(1.0)],"derivedFrom":[makeQuery(id+"F3.boolean.opBoolean","SPLIT",FACE,{"disambiguationData":[OD(0.0)],"derivedFrom":makeQuery(id+"F1.opExtrude","SWEPT_FACE",FACE,{"disambiguationData":[OSD([sQuery(id+"F0.wireOp",EDGE,"E1")])]})}),makeQuery(id+"F9.opSweep","SWEPT_FACE",FACE,{"disambiguationData":[OSD([sQuery(id+"F6.wireOp",EDGE,"E40"),sQuery(id+"F8.wireOp",EDGE,"E59")])]})]});
            var Q32;
            Q32=makeQuery(id+"F9.boolean.opBoolean","INTERSECT",EDGE,{"disambiguationData":[OD(1.0)],"derivedFrom":[makeQuery(id+"F3.boolean.opBoolean","SPLIT",FACE,{"disambiguationData":[OD(0.0)],"derivedFrom":makeQuery(id+"F1.opExtrude","SWEPT_FACE",FACE,{"disambiguationData":[OSD([sQuery(id+"F0.wireOp",EDGE,"E1")])]})}),makeQuery(id+"F9.opSweep","SWEPT_FACE",FACE,{"disambiguationData":[OSD([sQuery(id+"F6.wireOp",EDGE,"E41"),sQuery(id+"F8.wireOp",EDGE,"E59")])]})]});
            var Q33;
            Q33=makeQuery(id+"F9.boolean.opBoolean","INTERSECT",EDGE,{"disambiguationData":[OD(1.0)],"derivedFrom":[makeQuery(id+"F3.boolean.opBoolean","SPLIT",FACE,{"disambiguationData":[OD(0.0)],"derivedFrom":makeQuery(id+"F1.opExtrude","SWEPT_FACE",FACE,{"disambiguationData":[OSD([sQuery(id+"F0.wireOp",EDGE,"E1")])]})}),makeQuery(id+"F9.opSweep","SWEPT_FACE",FACE,{"disambiguationData":[OSD([sQuery(id+"F6.wireOp",EDGE,"E42"),sQuery(id+"F8.wireOp",EDGE,"E59")])]})]});
            var Q34;
            Q34=makeQuery(id+"F9.boolean.opBoolean","INTERSECT",EDGE,{"disambiguationData":[OD(1.0)],"derivedFrom":[makeQuery(id+"F3.boolean.opBoolean","SPLIT",FACE,{"disambiguationData":[OD(0.0)],"derivedFrom":makeQuery(id+"F1.opExtrude","SWEPT_FACE",FACE,{"disambiguationData":[OSD([sQuery(id+"F0.wireOp",EDGE,"E1")])]})}),makeQuery(id+"F9.opSweep","SWEPT_FACE",FACE,{"disambiguationData":[OSD([sQuery(id+"F6.wireOp",EDGE,"E43"),sQuery(id+"F8.wireOp",EDGE,"E59")])]})]});
            var Q35;
            Q35=makeQuery(id+"F9.boolean.opBoolean","INTERSECT",EDGE,{"disambiguationData":[OD(1.0)],"derivedFrom":[makeQuery(id+"F3.boolean.opBoolean","SPLIT",FACE,{"disambiguationData":[OD(0.0)],"derivedFrom":makeQuery(id+"F1.opExtrude","SWEPT_FACE",FACE,{"disambiguationData":[OSD([sQuery(id+"F0.wireOp",EDGE,"E1")])]})}),makeQuery(id+"F9.opSweep","SWEPT_FACE",FACE,{"disambiguationData":[OSD([sQuery(id+"F6.wireOp",EDGE,"E44"),sQuery(id+"F8.wireOp",EDGE,"E59")])]})]});
            var Q36;
            Q36=makeQuery(id+"F9.boolean.opBoolean","INTERSECT",EDGE,{"disambiguationData":[OD(1.0)],"derivedFrom":[makeQuery(id+"F3.boolean.opBoolean","SPLIT",FACE,{"disambiguationData":[OD(0.0)],"derivedFrom":makeQuery(id+"F1.opExtrude","SWEPT_FACE",FACE,{"disambiguationData":[OSD([sQuery(id+"F0.wireOp",EDGE,"E1")])]})}),makeQuery(id+"F9.opSweep","SWEPT_FACE",FACE,{"disambiguationData":[OSD([sQuery(id+"F6.wireOp",EDGE,"E45"),sQuery(id+"F8.wireOp",EDGE,"E59")])]})]});
            var Q37;
            Q37=makeQuery(id+"F9.boolean.opBoolean","INTERSECT",EDGE,{"disambiguationData":[OD(1.0)],"derivedFrom":[makeQuery(id+"F3.boolean.opBoolean","SPLIT",FACE,{"disambiguationData":[OD(0.0)],"derivedFrom":makeQuery(id+"F1.opExtrude","SWEPT_FACE",FACE,{"disambiguationData":[OSD([sQuery(id+"F0.wireOp",EDGE,"E1")])]})}),makeQuery(id+"F9.opSweep","SWEPT_FACE",FACE,{"disambiguationData":[OSD([sQuery(id+"F6.wireOp",EDGE,"E46"),sQuery(id+"F8.wireOp",EDGE,"E59")])]})]});
            var Q38;
            Q38=makeQuery(id+"F9.boolean.opBoolean","INTERSECT",EDGE,{"disambiguationData":[OD(1.0)],"derivedFrom":[makeQuery(id+"F3.boolean.opBoolean","SPLIT",FACE,{"disambiguationData":[OD(0.0)],"derivedFrom":makeQuery(id+"F1.opExtrude","SWEPT_FACE",FACE,{"disambiguationData":[OSD([sQuery(id+"F0.wireOp",EDGE,"E1")])]})}),makeQuery(id+"F9.opSweep","SWEPT_FACE",FACE,{"disambiguationData":[OSD([sQuery(id+"F6.wireOp",EDGE,"E47"),sQuery(id+"F8.wireOp",EDGE,"E59")])]})]});
            var Q39;
            Q39=makeQuery(id+"F9.boolean.opBoolean","INTERSECT",EDGE,{"disambiguationData":[OD(1.0)],"derivedFrom":[makeQuery(id+"F3.boolean.opBoolean","SPLIT",FACE,{"disambiguationData":[OD(0.0)],"derivedFrom":makeQuery(id+"F1.opExtrude","SWEPT_FACE",FACE,{"disambiguationData":[OSD([sQuery(id+"F0.wireOp",EDGE,"E1")])]})}),makeQuery(id+"F9.opSweep","SWEPT_FACE",FACE,{"disambiguationData":[OSD([sQuery(id+"F6.wireOp",EDGE,"E48"),sQuery(id+"F8.wireOp",EDGE,"E59")])]})]});
            var Q40;
            Q40=makeQuery(id+"F9.boolean.opBoolean","INTERSECT",EDGE,{"disambiguationData":[OD(1.0)],"derivedFrom":[makeQuery(id+"F3.boolean.opBoolean","SPLIT",FACE,{"disambiguationData":[OD(0.0)],"derivedFrom":makeQuery(id+"F1.opExtrude","SWEPT_FACE",FACE,{"disambiguationData":[OSD([sQuery(id+"F0.wireOp",EDGE,"E1")])]})}),makeQuery(id+"F9.opSweep","SWEPT_FACE",FACE,{"disambiguationData":[OSD([sQuery(id+"F6.wireOp",EDGE,"E49"),sQuery(id+"F8.wireOp",EDGE,"E59")])]})]});
            var Q41;
            Q41=makeQuery(id+"F9.boolean.opBoolean","INTERSECT",EDGE,{"disambiguationData":[OD(1.0)],"derivedFrom":[makeQuery(id+"F3.boolean.opBoolean","SPLIT",FACE,{"disambiguationData":[OD(0.0)],"derivedFrom":makeQuery(id+"F1.opExtrude","SWEPT_FACE",FACE,{"disambiguationData":[OSD([sQuery(id+"F0.wireOp",EDGE,"E1")])]})}),makeQuery(id+"F9.opSweep","SWEPT_FACE",FACE,{"disambiguationData":[OSD([sQuery(id+"F6.wireOp",EDGE,"E50"),sQuery(id+"F8.wireOp",EDGE,"E59")])]})]});
            var Q42;
            Q42=makeQuery(id+"F9.boolean.opBoolean","INTERSECT",EDGE,{"disambiguationData":[OD(1.0)],"derivedFrom":[makeQuery(id+"F3.boolean.opBoolean","SPLIT",FACE,{"disambiguationData":[OD(0.0)],"derivedFrom":makeQuery(id+"F1.opExtrude","SWEPT_FACE",FACE,{"disambiguationData":[OSD([sQuery(id+"F0.wireOp",EDGE,"E1")])]})}),makeQuery(id+"F9.opSweep","SWEPT_FACE",FACE,{"disambiguationData":[OSD([sQuery(id+"F6.wireOp",EDGE,"E51"),sQuery(id+"F8.wireOp",EDGE,"E59")])]})]});
            var Q43;
            Q43=makeQuery(id+"F9.boolean.opBoolean","INTERSECT",EDGE,{"disambiguationData":[OD(1.0)],"derivedFrom":[makeQuery(id+"F3.boolean.opBoolean","SPLIT",FACE,{"disambiguationData":[OD(0.0)],"derivedFrom":makeQuery(id+"F1.opExtrude","SWEPT_FACE",FACE,{"disambiguationData":[OSD([sQuery(id+"F0.wireOp",EDGE,"E1")])]})}),makeQuery(id+"F9.opSweep","SWEPT_FACE",FACE,{"disambiguationData":[OSD([sQuery(id+"F6.wireOp",EDGE,"E52"),sQuery(id+"F8.wireOp",EDGE,"E59")])]})]});
            var Q44;
            Q44=makeQuery(id+"F9.boolean.opBoolean","INTERSECT",EDGE,{"disambiguationData":[OD(1.0)],"derivedFrom":[makeQuery(id+"F3.boolean.opBoolean","SPLIT",FACE,{"disambiguationData":[OD(0.0)],"derivedFrom":makeQuery(id+"F1.opExtrude","SWEPT_FACE",FACE,{"disambiguationData":[OSD([sQuery(id+"F0.wireOp",EDGE,"E1")])]})}),makeQuery(id+"F9.opSweep","SWEPT_FACE",FACE,{"disambiguationData":[OSD([sQuery(id+"F6.wireOp",EDGE,"E53"),sQuery(id+"F8.wireOp",EDGE,"E59")])]})]});
            var Q45;
            Q45=makeQuery(id+"F9.boolean.opBoolean","INTERSECT",EDGE,{"disambiguationData":[OD(1.0)],"derivedFrom":[makeQuery(id+"F3.boolean.opBoolean","SPLIT",FACE,{"disambiguationData":[OD(0.0)],"derivedFrom":makeQuery(id+"F1.opExtrude","SWEPT_FACE",FACE,{"disambiguationData":[OSD([sQuery(id+"F0.wireOp",EDGE,"E1")])]})}),makeQuery(id+"F9.opSweep","SWEPT_FACE",FACE,{"disambiguationData":[OSD([sQuery(id+"F6.wireOp",EDGE,"E54"),sQuery(id+"F8.wireOp",EDGE,"E59")])]})]});
            var Q46;
            Q46=makeQuery(id+"F9.boolean.opBoolean","INTERSECT",EDGE,{"disambiguationData":[OD(1.0)],"derivedFrom":[makeQuery(id+"F3.boolean.opBoolean","SPLIT",FACE,{"disambiguationData":[OD(0.0)],"derivedFrom":makeQuery(id+"F1.opExtrude","SWEPT_FACE",FACE,{"disambiguationData":[OSD([sQuery(id+"F0.wireOp",EDGE,"E1")])]})}),makeQuery(id+"F9.opSweep","SWEPT_FACE",FACE,{"disambiguationData":[OSD([sQuery(id+"F6.wireOp",EDGE,"E55"),sQuery(id+"F8.wireOp",EDGE,"E59")])]})]});
            var Q47;
            Q47=makeQuery(id+"F9.boolean.opBoolean","INTERSECT",EDGE,{"disambiguationData":[OD(1.0)],"derivedFrom":[makeQuery(id+"F3.boolean.opBoolean","SPLIT",FACE,{"disambiguationData":[OD(0.0)],"derivedFrom":makeQuery(id+"F1.opExtrude","SWEPT_FACE",FACE,{"disambiguationData":[OSD([sQuery(id+"F0.wireOp",EDGE,"E1")])]})}),makeQuery(id+"F9.opSweep","SWEPT_FACE",FACE,{"disambiguationData":[OSD([sQuery(id+"F6.wireOp",EDGE,"E56"),sQuery(id+"F8.wireOp",EDGE,"E59")])]})]});
            var Q48;
            Q48=makeQuery(id+"F9.boolean.opBoolean","INTERSECT",EDGE,{"disambiguationData":[OD(1.0)],"derivedFrom":[makeQuery(id+"F3.boolean.opBoolean","SPLIT",FACE,{"disambiguationData":[OD(0.0)],"derivedFrom":makeQuery(id+"F1.opExtrude","SWEPT_FACE",FACE,{"disambiguationData":[OSD([sQuery(id+"F0.wireOp",EDGE,"E1")])]})}),makeQuery(id+"F9.opSweep","SWEPT_FACE",FACE,{"disambiguationData":[OSD([sQuery(id+"F6.wireOp",EDGE,"E57"),sQuery(id+"F8.wireOp",EDGE,"E59")])]})]});
            var Q49;
            Q49=makeQuery(id+"F9.boolean.opBoolean","INTERSECT",EDGE,{"disambiguationData":[OD(0.0)],"derivedFrom":[makeQuery(id+"F3.boolean.opBoolean","SPLIT",FACE,{"disambiguationData":[OD(0.0)],"derivedFrom":makeQuery(id+"F1.opExtrude","SWEPT_FACE",FACE,{"disambiguationData":[OSD([sQuery(id+"F0.wireOp",EDGE,"E1")])]})}),makeQuery(id+"F9.opSweep","SWEPT_FACE",FACE,{"disambiguationData":[OSD([sQuery(id+"F6.wireOp",EDGE,"E56"),sQuery(id+"F8.wireOp",EDGE,"E59")])]})]});
            var Q50;
            Q50=makeQuery(id+"F9.boolean.opBoolean","INTERSECT",EDGE,{"disambiguationData":[OD(0.0)],"derivedFrom":[makeQuery(id+"F3.boolean.opBoolean","SPLIT",FACE,{"disambiguationData":[OD(0.0)],"derivedFrom":makeQuery(id+"F1.opExtrude","SWEPT_FACE",FACE,{"disambiguationData":[OSD([sQuery(id+"F0.wireOp",EDGE,"E1")])]})}),makeQuery(id+"F9.opSweep","SWEPT_FACE",FACE,{"disambiguationData":[OSD([sQuery(id+"F6.wireOp",EDGE,"E55"),sQuery(id+"F8.wireOp",EDGE,"E59")])]})]});
            var Q51;
            Q51=makeQuery(id+"F9.boolean.opBoolean","INTERSECT",EDGE,{"disambiguationData":[OD(0.0)],"derivedFrom":[makeQuery(id+"F3.boolean.opBoolean","SPLIT",FACE,{"disambiguationData":[OD(0.0)],"derivedFrom":makeQuery(id+"F1.opExtrude","SWEPT_FACE",FACE,{"disambiguationData":[OSD([sQuery(id+"F0.wireOp",EDGE,"E1")])]})}),makeQuery(id+"F9.opSweep","SWEPT_FACE",FACE,{"disambiguationData":[OSD([sQuery(id+"F6.wireOp",EDGE,"E54"),sQuery(id+"F8.wireOp",EDGE,"E59")])]})]});
            var Q52;
            Q52=makeQuery(id+"F9.boolean.opBoolean","INTERSECT",EDGE,{"disambiguationData":[OD(0.0)],"derivedFrom":[makeQuery(id+"F3.boolean.opBoolean","SPLIT",FACE,{"disambiguationData":[OD(0.0)],"derivedFrom":makeQuery(id+"F1.opExtrude","SWEPT_FACE",FACE,{"disambiguationData":[OSD([sQuery(id+"F0.wireOp",EDGE,"E1")])]})}),makeQuery(id+"F9.opSweep","SWEPT_FACE",FACE,{"disambiguationData":[OSD([sQuery(id+"F6.wireOp",EDGE,"E53"),sQuery(id+"F8.wireOp",EDGE,"E59")])]})]});
            var Q53;
            Q53=makeQuery(id+"F9.boolean.opBoolean","INTERSECT",EDGE,{"disambiguationData":[OD(0.0)],"derivedFrom":[makeQuery(id+"F3.boolean.opBoolean","SPLIT",FACE,{"disambiguationData":[OD(0.0)],"derivedFrom":makeQuery(id+"F1.opExtrude","SWEPT_FACE",FACE,{"disambiguationData":[OSD([sQuery(id+"F0.wireOp",EDGE,"E1")])]})}),makeQuery(id+"F9.opSweep","SWEPT_FACE",FACE,{"disambiguationData":[OSD([sQuery(id+"F6.wireOp",EDGE,"E52"),sQuery(id+"F8.wireOp",EDGE,"E59")])]})]});
            var Q54;
            Q54=makeQuery(id+"F9.boolean.opBoolean","INTERSECT",EDGE,{"disambiguationData":[OD(0.0)],"derivedFrom":[makeQuery(id+"F3.boolean.opBoolean","SPLIT",FACE,{"disambiguationData":[OD(0.0)],"derivedFrom":makeQuery(id+"F1.opExtrude","SWEPT_FACE",FACE,{"disambiguationData":[OSD([sQuery(id+"F0.wireOp",EDGE,"E1")])]})}),makeQuery(id+"F9.opSweep","SWEPT_FACE",FACE,{"disambiguationData":[OSD([sQuery(id+"F6.wireOp",EDGE,"E51"),sQuery(id+"F8.wireOp",EDGE,"E59")])]})]});
            var Q55;
            Q55=makeQuery(id+"F9.boolean.opBoolean","INTERSECT",EDGE,{"disambiguationData":[OD(0.0)],"derivedFrom":[makeQuery(id+"F3.boolean.opBoolean","SPLIT",FACE,{"disambiguationData":[OD(0.0)],"derivedFrom":makeQuery(id+"F1.opExtrude","SWEPT_FACE",FACE,{"disambiguationData":[OSD([sQuery(id+"F0.wireOp",EDGE,"E1")])]})}),makeQuery(id+"F9.opSweep","SWEPT_FACE",FACE,{"disambiguationData":[OSD([sQuery(id+"F6.wireOp",EDGE,"E50"),sQuery(id+"F8.wireOp",EDGE,"E59")])]})]});
            var Q56;
            Q56=makeQuery(id+"F9.boolean.opBoolean","INTERSECT",EDGE,{"disambiguationData":[OD(0.0)],"derivedFrom":[makeQuery(id+"F3.boolean.opBoolean","SPLIT",FACE,{"disambiguationData":[OD(0.0)],"derivedFrom":makeQuery(id+"F1.opExtrude","SWEPT_FACE",FACE,{"disambiguationData":[OSD([sQuery(id+"F0.wireOp",EDGE,"E1")])]})}),makeQuery(id+"F9.opSweep","SWEPT_FACE",FACE,{"disambiguationData":[OSD([sQuery(id+"F6.wireOp",EDGE,"E49"),sQuery(id+"F8.wireOp",EDGE,"E59")])]})]});
            var Q57;
            Q57=makeQuery(id+"F9.boolean.opBoolean","INTERSECT",EDGE,{"disambiguationData":[OD(0.0)],"derivedFrom":[makeQuery(id+"F3.boolean.opBoolean","SPLIT",FACE,{"disambiguationData":[OD(0.0)],"derivedFrom":makeQuery(id+"F1.opExtrude","SWEPT_FACE",FACE,{"disambiguationData":[OSD([sQuery(id+"F0.wireOp",EDGE,"E1")])]})}),makeQuery(id+"F9.opSweep","SWEPT_FACE",FACE,{"disambiguationData":[OSD([sQuery(id+"F6.wireOp",EDGE,"E48"),sQuery(id+"F8.wireOp",EDGE,"E59")])]})]});
            var Q58;
            Q58=makeQuery(id+"F9.boolean.opBoolean","INTERSECT",EDGE,{"disambiguationData":[OD(0.0)],"derivedFrom":[makeQuery(id+"F3.boolean.opBoolean","SPLIT",FACE,{"disambiguationData":[OD(0.0)],"derivedFrom":makeQuery(id+"F1.opExtrude","SWEPT_FACE",FACE,{"disambiguationData":[OSD([sQuery(id+"F0.wireOp",EDGE,"E1")])]})}),makeQuery(id+"F9.opSweep","SWEPT_FACE",FACE,{"disambiguationData":[OSD([sQuery(id+"F6.wireOp",EDGE,"E47"),sQuery(id+"F8.wireOp",EDGE,"E59")])]})]});
            var Q59;
            Q59=makeQuery(id+"F9.boolean.opBoolean","INTERSECT",EDGE,{"disambiguationData":[OD(0.0)],"derivedFrom":[makeQuery(id+"F3.boolean.opBoolean","SPLIT",FACE,{"disambiguationData":[OD(0.0)],"derivedFrom":makeQuery(id+"F1.opExtrude","SWEPT_FACE",FACE,{"disambiguationData":[OSD([sQuery(id+"F0.wireOp",EDGE,"E1")])]})}),makeQuery(id+"F9.opSweep","SWEPT_FACE",FACE,{"disambiguationData":[OSD([sQuery(id+"F6.wireOp",EDGE,"E46"),sQuery(id+"F8.wireOp",EDGE,"E59")])]})]});
            var Q60;
            Q60=makeQuery(id+"F9.boolean.opBoolean","INTERSECT",EDGE,{"disambiguationData":[OD(0.0)],"derivedFrom":[makeQuery(id+"F3.boolean.opBoolean","SPLIT",FACE,{"disambiguationData":[OD(0.0)],"derivedFrom":makeQuery(id+"F1.opExtrude","SWEPT_FACE",FACE,{"disambiguationData":[OSD([sQuery(id+"F0.wireOp",EDGE,"E1")])]})}),makeQuery(id+"F9.opSweep","SWEPT_FACE",FACE,{"disambiguationData":[OSD([sQuery(id+"F6.wireOp",EDGE,"E45"),sQuery(id+"F8.wireOp",EDGE,"E59")])]})]});
            var Q61;
            Q61=makeQuery(id+"F9.boolean.opBoolean","INTERSECT",EDGE,{"disambiguationData":[OD(0.0)],"derivedFrom":[makeQuery(id+"F3.boolean.opBoolean","SPLIT",FACE,{"disambiguationData":[OD(0.0)],"derivedFrom":makeQuery(id+"F1.opExtrude","SWEPT_FACE",FACE,{"disambiguationData":[OSD([sQuery(id+"F0.wireOp",EDGE,"E1")])]})}),makeQuery(id+"F9.opSweep","SWEPT_FACE",FACE,{"disambiguationData":[OSD([sQuery(id+"F6.wireOp",EDGE,"E44"),sQuery(id+"F8.wireOp",EDGE,"E59")])]})]});
            var Q62;
            Q62=makeQuery(id+"F9.boolean.opBoolean","INTERSECT",EDGE,{"disambiguationData":[OD(0.0)],"derivedFrom":[makeQuery(id+"F3.boolean.opBoolean","SPLIT",FACE,{"disambiguationData":[OD(0.0)],"derivedFrom":makeQuery(id+"F1.opExtrude","SWEPT_FACE",FACE,{"disambiguationData":[OSD([sQuery(id+"F0.wireOp",EDGE,"E1")])]})}),makeQuery(id+"F9.opSweep","SWEPT_FACE",FACE,{"disambiguationData":[OSD([sQuery(id+"F6.wireOp",EDGE,"E43"),sQuery(id+"F8.wireOp",EDGE,"E59")])]})]});
            var Q63;
            Q63=makeQuery(id+"F9.boolean.opBoolean","INTERSECT",EDGE,{"disambiguationData":[OD(0.0)],"derivedFrom":[makeQuery(id+"F3.boolean.opBoolean","SPLIT",FACE,{"disambiguationData":[OD(0.0)],"derivedFrom":makeQuery(id+"F1.opExtrude","SWEPT_FACE",FACE,{"disambiguationData":[OSD([sQuery(id+"F0.wireOp",EDGE,"E1")])]})}),makeQuery(id+"F9.opSweep","SWEPT_FACE",FACE,{"disambiguationData":[OSD([sQuery(id+"F6.wireOp",EDGE,"E42"),sQuery(id+"F8.wireOp",EDGE,"E59")])]})]});
            var Q64;
            Q64=makeQuery(id+"F9.boolean.opBoolean","INTERSECT",EDGE,{"disambiguationData":[OD(0.0)],"derivedFrom":[makeQuery(id+"F3.boolean.opBoolean","SPLIT",FACE,{"disambiguationData":[OD(0.0)],"derivedFrom":makeQuery(id+"F1.opExtrude","SWEPT_FACE",FACE,{"disambiguationData":[OSD([sQuery(id+"F0.wireOp",EDGE,"E1")])]})}),makeQuery(id+"F9.opSweep","SWEPT_FACE",FACE,{"disambiguationData":[OSD([sQuery(id+"F6.wireOp",EDGE,"E41"),sQuery(id+"F8.wireOp",EDGE,"E59")])]})]});
            var Q65;
            Q65=makeQuery(id+"F9.boolean.opBoolean","INTERSECT",EDGE,{"disambiguationData":[OD(0.0)],"derivedFrom":[makeQuery(id+"F3.boolean.opBoolean","SPLIT",FACE,{"disambiguationData":[OD(0.0)],"derivedFrom":makeQuery(id+"F1.opExtrude","SWEPT_FACE",FACE,{"disambiguationData":[OSD([sQuery(id+"F0.wireOp",EDGE,"E1")])]})}),makeQuery(id+"F9.opSweep","SWEPT_FACE",FACE,{"disambiguationData":[OSD([sQuery(id+"F6.wireOp",EDGE,"E40"),sQuery(id+"F8.wireOp",EDGE,"E59")])]})]});
            var Q66;
            Q66=makeQuery(id+"F9.boolean.opBoolean","INTERSECT",EDGE,{"disambiguationData":[OD(0.0)],"derivedFrom":[makeQuery(id+"F3.boolean.opBoolean","SPLIT",FACE,{"disambiguationData":[OD(0.0)],"derivedFrom":makeQuery(id+"F1.opExtrude","SWEPT_FACE",FACE,{"disambiguationData":[OSD([sQuery(id+"F0.wireOp",EDGE,"E1")])]})}),makeQuery(id+"F9.opSweep","SWEPT_FACE",FACE,{"disambiguationData":[OSD([sQuery(id+"F6.wireOp",EDGE,"E39"),sQuery(id+"F8.wireOp",EDGE,"E59")])]})]});
            var Q67;
            Q67=makeQuery(id+"F9.boolean.opBoolean","INTERSECT",EDGE,{"disambiguationData":[OD(0.0)],"derivedFrom":[makeQuery(id+"F3.boolean.opBoolean","SPLIT",FACE,{"disambiguationData":[OD(0.0)],"derivedFrom":makeQuery(id+"F1.opExtrude","SWEPT_FACE",FACE,{"disambiguationData":[OSD([sQuery(id+"F0.wireOp",EDGE,"E1")])]})}),makeQuery(id+"F9.opSweep","SWEPT_FACE",FACE,{"disambiguationData":[OSD([sQuery(id+"F6.wireOp",EDGE,"E38"),sQuery(id+"F8.wireOp",EDGE,"E59")])]})]});
            var Q68;
            Q68=makeQuery(id+"F9.boolean.opBoolean","INTERSECT",EDGE,{"disambiguationData":[OD(0.0)],"derivedFrom":[makeQuery(id+"F3.boolean.opBoolean","SPLIT",FACE,{"disambiguationData":[OD(0.0)],"derivedFrom":makeQuery(id+"F1.opExtrude","SWEPT_FACE",FACE,{"disambiguationData":[OSD([sQuery(id+"F0.wireOp",EDGE,"E1")])]})}),makeQuery(id+"F9.opSweep","SWEPT_FACE",FACE,{"disambiguationData":[OSD([sQuery(id+"F6.wireOp",EDGE,"E37"),sQuery(id+"F8.wireOp",EDGE,"E59")])]})]});
            var Q69;
            Q69=makeQuery(id+"F9.boolean.opBoolean","INTERSECT",EDGE,{"disambiguationData":[OD(0.0)],"derivedFrom":[makeQuery(id+"F3.boolean.opBoolean","SPLIT",FACE,{"disambiguationData":[OD(0.0)],"derivedFrom":makeQuery(id+"F1.opExtrude","SWEPT_FACE",FACE,{"disambiguationData":[OSD([sQuery(id+"F0.wireOp",EDGE,"E1")])]})}),makeQuery(id+"F9.opSweep","SWEPT_FACE",FACE,{"disambiguationData":[OSD([sQuery(id+"F6.wireOp",EDGE,"E36"),sQuery(id+"F8.wireOp",EDGE,"E59")])]})]});
            var Q70;
            Q70=makeQuery(id+"F9.boolean.opBoolean","INTERSECT",EDGE,{"disambiguationData":[OD(0.0)],"derivedFrom":[makeQuery(id+"F3.boolean.opBoolean","SPLIT",FACE,{"disambiguationData":[OD(0.0)],"derivedFrom":makeQuery(id+"F1.opExtrude","SWEPT_FACE",FACE,{"disambiguationData":[OSD([sQuery(id+"F0.wireOp",EDGE,"E1")])]})}),makeQuery(id+"F9.opSweep","SWEPT_FACE",FACE,{"disambiguationData":[OSD([sQuery(id+"F6.wireOp",EDGE,"E35"),sQuery(id+"F8.wireOp",EDGE,"E59")])]})]});
            var Q71;
            Q71=makeQuery(id+"F9.boolean.opBoolean","INTERSECT",EDGE,{"disambiguationData":[OD(0.0)],"derivedFrom":[makeQuery(id+"F3.boolean.opBoolean","SPLIT",FACE,{"disambiguationData":[OD(0.0)],"derivedFrom":makeQuery(id+"F1.opExtrude","SWEPT_FACE",FACE,{"disambiguationData":[OSD([sQuery(id+"F0.wireOp",EDGE,"E1")])]})}),makeQuery(id+"F9.opSweep","SWEPT_FACE",FACE,{"disambiguationData":[OSD([sQuery(id+"F6.wireOp",EDGE,"E34"),sQuery(id+"F8.wireOp",EDGE,"E59")])]})]});
            var Q72;
            Q72=makeQuery(id+"F9.boolean.opBoolean","INTERSECT",EDGE,{"disambiguationData":[OD(0.0)],"derivedFrom":[makeQuery(id+"F3.boolean.opBoolean","SPLIT",FACE,{"disambiguationData":[OD(0.0)],"derivedFrom":makeQuery(id+"F1.opExtrude","SWEPT_FACE",FACE,{"disambiguationData":[OSD([sQuery(id+"F0.wireOp",EDGE,"E1")])]})}),makeQuery(id+"F9.opSweep","SWEPT_FACE",FACE,{"disambiguationData":[OSD([sQuery(id+"F6.wireOp",EDGE,"E33"),sQuery(id+"F8.wireOp",EDGE,"E59")])]})]});
            var Q73;
            Q73=makeQuery(id+"F9.boolean.opBoolean","INTERSECT",EDGE,{"disambiguationData":[OD(0.0)],"derivedFrom":[makeQuery(id+"F3.boolean.opBoolean","SPLIT",FACE,{"disambiguationData":[OD(0.0)],"derivedFrom":makeQuery(id+"F1.opExtrude","SWEPT_FACE",FACE,{"disambiguationData":[OSD([sQuery(id+"F0.wireOp",EDGE,"E1")])]})}),makeQuery(id+"F9.opSweep","SWEPT_FACE",FACE,{"disambiguationData":[OSD([sQuery(id+"F6.wireOp",EDGE,"E32"),sQuery(id+"F8.wireOp",EDGE,"E59")])]})]});
            var Q74;
            Q74=makeQuery(id+"F9.boolean.opBoolean","INTERSECT",EDGE,{"disambiguationData":[OD(0.0)],"derivedFrom":[makeQuery(id+"F3.boolean.opBoolean","SPLIT",FACE,{"disambiguationData":[OD(0.0)],"derivedFrom":makeQuery(id+"F1.opExtrude","SWEPT_FACE",FACE,{"disambiguationData":[OSD([sQuery(id+"F0.wireOp",EDGE,"E1")])]})}),makeQuery(id+"F9.opSweep","SWEPT_FACE",FACE,{"disambiguationData":[OSD([sQuery(id+"F6.wireOp",EDGE,"E31"),sQuery(id+"F8.wireOp",EDGE,"E59")])]})]});
            var Q75;
            Q75=makeQuery(id+"F9.boolean.opBoolean","INTERSECT",EDGE,{"disambiguationData":[OD(0.0)],"derivedFrom":[makeQuery(id+"F3.boolean.opBoolean","SPLIT",FACE,{"disambiguationData":[OD(0.0)],"derivedFrom":makeQuery(id+"F1.opExtrude","SWEPT_FACE",FACE,{"disambiguationData":[OSD([sQuery(id+"F0.wireOp",EDGE,"E1")])]})}),makeQuery(id+"F9.opSweep","SWEPT_FACE",FACE,{"disambiguationData":[OSD([sQuery(id+"F6.wireOp",EDGE,"E30"),sQuery(id+"F8.wireOp",EDGE,"E59")])]})]});
            var Q76;
            Q76=makeQuery(id+"F9.boolean.opBoolean","INTERSECT",EDGE,{"disambiguationData":[OD(0.0)],"derivedFrom":[makeQuery(id+"F3.boolean.opBoolean","SPLIT",FACE,{"disambiguationData":[OD(0.0)],"derivedFrom":makeQuery(id+"F1.opExtrude","SWEPT_FACE",FACE,{"disambiguationData":[OSD([sQuery(id+"F0.wireOp",EDGE,"E1")])]})}),makeQuery(id+"F9.opSweep","SWEPT_FACE",FACE,{"disambiguationData":[OSD([sQuery(id+"F6.wireOp",EDGE,"E29"),sQuery(id+"F8.wireOp",EDGE,"E59")])]})]});
            var Q77;
            Q77=makeQuery(id+"F9.boolean.opBoolean","INTERSECT",EDGE,{"disambiguationData":[OD(0.0)],"derivedFrom":[makeQuery(id+"F3.boolean.opBoolean","SPLIT",FACE,{"disambiguationData":[OD(0.0)],"derivedFrom":makeQuery(id+"F1.opExtrude","SWEPT_FACE",FACE,{"disambiguationData":[OSD([sQuery(id+"F0.wireOp",EDGE,"E1")])]})}),makeQuery(id+"F9.opSweep","SWEPT_FACE",FACE,{"disambiguationData":[OSD([sQuery(id+"F6.wireOp",EDGE,"E28"),sQuery(id+"F8.wireOp",EDGE,"E59")])]})]});
            var Q78;
            Q78=makeQuery(id+"F9.boolean.opBoolean","INTERSECT",EDGE,{"disambiguationData":[OD(0.0)],"derivedFrom":[makeQuery(id+"F3.boolean.opBoolean","SPLIT",FACE,{"disambiguationData":[OD(0.0)],"derivedFrom":makeQuery(id+"F1.opExtrude","SWEPT_FACE",FACE,{"disambiguationData":[OSD([sQuery(id+"F0.wireOp",EDGE,"E1")])]})}),makeQuery(id+"F9.opSweep","SWEPT_FACE",FACE,{"disambiguationData":[OSD([sQuery(id+"F6.wireOp",EDGE,"E27"),sQuery(id+"F8.wireOp",EDGE,"E59")])]})]});
            var Q79;
            Q79=makeQuery(id+"F9.boolean.opBoolean","INTERSECT",EDGE,{"disambiguationData":[OD(0.0)],"derivedFrom":[makeQuery(id+"F3.boolean.opBoolean","SPLIT",FACE,{"disambiguationData":[OD(0.0)],"derivedFrom":makeQuery(id+"F1.opExtrude","SWEPT_FACE",FACE,{"disambiguationData":[OSD([sQuery(id+"F0.wireOp",EDGE,"E1")])]})}),makeQuery(id+"F9.opSweep","SWEPT_FACE",FACE,{"disambiguationData":[OSD([sQuery(id+"F6.wireOp",EDGE,"E26"),sQuery(id+"F8.wireOp",EDGE,"E59")])]})]});
            var Q80;
            Q80=makeQuery(id+"F9.boolean.opBoolean","INTERSECT",EDGE,{"disambiguationData":[OD(0.0)],"derivedFrom":[makeQuery(id+"F3.boolean.opBoolean","SPLIT",FACE,{"disambiguationData":[OD(0.0)],"derivedFrom":makeQuery(id+"F1.opExtrude","SWEPT_FACE",FACE,{"disambiguationData":[OSD([sQuery(id+"F0.wireOp",EDGE,"E1")])]})}),makeQuery(id+"F9.opSweep","SWEPT_FACE",FACE,{"disambiguationData":[OSD([sQuery(id+"F6.wireOp",EDGE,"E25"),sQuery(id+"F8.wireOp",EDGE,"E59")])]})]});
            var Q81;
            Q81=makeQuery(id+"F9.boolean.opBoolean","INTERSECT",EDGE,{"disambiguationData":[OD(0.0)],"derivedFrom":[makeQuery(id+"F3.boolean.opBoolean","SPLIT",FACE,{"disambiguationData":[OD(0.0)],"derivedFrom":makeQuery(id+"F1.opExtrude","SWEPT_FACE",FACE,{"disambiguationData":[OSD([sQuery(id+"F0.wireOp",EDGE,"E1")])]})}),makeQuery(id+"F9.opSweep","SWEPT_FACE",FACE,{"disambiguationData":[OSD([sQuery(id+"F6.wireOp",EDGE,"E24"),sQuery(id+"F8.wireOp",EDGE,"E59")])]})]});
            var Q82;
            Q82=makeQuery(id+"F9.boolean.opBoolean","INTERSECT",EDGE,{"disambiguationData":[OD(0.0)],"derivedFrom":[makeQuery(id+"F3.boolean.opBoolean","SPLIT",FACE,{"disambiguationData":[OD(0.0)],"derivedFrom":makeQuery(id+"F1.opExtrude","SWEPT_FACE",FACE,{"disambiguationData":[OSD([sQuery(id+"F0.wireOp",EDGE,"E1")])]})}),makeQuery(id+"F9.opSweep","SWEPT_FACE",FACE,{"disambiguationData":[OSD([sQuery(id+"F6.wireOp",EDGE,"E23"),sQuery(id+"F8.wireOp",EDGE,"E59")])]})]});
            var Q83;
            Q83=makeQuery(id+"F9.boolean.opBoolean","INTERSECT",EDGE,{"disambiguationData":[OD(0.0)],"derivedFrom":[makeQuery(id+"F3.boolean.opBoolean","SPLIT",FACE,{"disambiguationData":[OD(0.0)],"derivedFrom":makeQuery(id+"F1.opExtrude","SWEPT_FACE",FACE,{"disambiguationData":[OSD([sQuery(id+"F0.wireOp",EDGE,"E1")])]})}),makeQuery(id+"F9.opSweep","SWEPT_FACE",FACE,{"disambiguationData":[OSD([sQuery(id+"F6.wireOp",EDGE,"E22"),sQuery(id+"F8.wireOp",EDGE,"E59")])]})]});
            var Q84;
            Q84=makeQuery(id+"F9.boolean.opBoolean","INTERSECT",EDGE,{"disambiguationData":[OD(0.0)],"derivedFrom":[makeQuery(id+"F3.boolean.opBoolean","SPLIT",FACE,{"disambiguationData":[OD(0.0)],"derivedFrom":makeQuery(id+"F1.opExtrude","SWEPT_FACE",FACE,{"disambiguationData":[OSD([sQuery(id+"F0.wireOp",EDGE,"E1")])]})}),makeQuery(id+"F9.opSweep","SWEPT_FACE",FACE,{"disambiguationData":[OSD([sQuery(id+"F6.wireOp",EDGE,"E21"),sQuery(id+"F8.wireOp",EDGE,"E59")])]})]});
            var Q85;
            Q85=makeQuery(id+"F9.boolean.opBoolean","INTERSECT",EDGE,{"disambiguationData":[OD(0.0)],"derivedFrom":[makeQuery(id+"F3.boolean.opBoolean","SPLIT",FACE,{"disambiguationData":[OD(0.0)],"derivedFrom":makeQuery(id+"F1.opExtrude","SWEPT_FACE",FACE,{"disambiguationData":[OSD([sQuery(id+"F0.wireOp",EDGE,"E1")])]})}),makeQuery(id+"F9.opSweep","SWEPT_FACE",FACE,{"disambiguationData":[OSD([sQuery(id+"F6.wireOp",EDGE,"E20"),sQuery(id+"F8.wireOp",EDGE,"E59")])]})]});
            var Q86;
            Q86=makeQuery(id+"F9.boolean.opBoolean","INTERSECT",EDGE,{"disambiguationData":[OD(0.0)],"derivedFrom":[makeQuery(id+"F3.boolean.opBoolean","SPLIT",FACE,{"disambiguationData":[OD(0.0)],"derivedFrom":makeQuery(id+"F1.opExtrude","SWEPT_FACE",FACE,{"disambiguationData":[OSD([sQuery(id+"F0.wireOp",EDGE,"E1")])]})}),makeQuery(id+"F9.opSweep","SWEPT_FACE",FACE,{"disambiguationData":[OSD([sQuery(id+"F6.wireOp",EDGE,"E19"),sQuery(id+"F8.wireOp",EDGE,"E59")])]})]});
            var Q87;
            Q87=makeQuery(id+"F9.boolean.opBoolean","INTERSECT",EDGE,{"disambiguationData":[OD(0.0)],"derivedFrom":[makeQuery(id+"F3.boolean.opBoolean","SPLIT",FACE,{"disambiguationData":[OD(0.0)],"derivedFrom":makeQuery(id+"F1.opExtrude","SWEPT_FACE",FACE,{"disambiguationData":[OSD([sQuery(id+"F0.wireOp",EDGE,"E1")])]})}),makeQuery(id+"F9.opSweep","SWEPT_FACE",FACE,{"disambiguationData":[OSD([sQuery(id+"F6.wireOp",EDGE,"E18"),sQuery(id+"F8.wireOp",EDGE,"E59")])]})]});
            var Q88;
            Q88=makeQuery(id+"F9.boolean.opBoolean","INTERSECT",EDGE,{"disambiguationData":[OD(0.0)],"derivedFrom":[makeQuery(id+"F3.boolean.opBoolean","SPLIT",FACE,{"disambiguationData":[OD(0.0)],"derivedFrom":makeQuery(id+"F1.opExtrude","SWEPT_FACE",FACE,{"disambiguationData":[OSD([sQuery(id+"F0.wireOp",EDGE,"E1")])]})}),makeQuery(id+"F9.opSweep","SWEPT_FACE",FACE,{"disambiguationData":[OSD([sQuery(id+"F6.wireOp",EDGE,"E17"),sQuery(id+"F8.wireOp",EDGE,"E59")])]})]});
            var Q89;
            Q89=makeQuery(id+"F9.boolean.opBoolean","INTERSECT",EDGE,{"disambiguationData":[OD(0.0)],"derivedFrom":[makeQuery(id+"F3.boolean.opBoolean","SPLIT",FACE,{"disambiguationData":[OD(0.0)],"derivedFrom":makeQuery(id+"F1.opExtrude","SWEPT_FACE",FACE,{"disambiguationData":[OSD([sQuery(id+"F0.wireOp",EDGE,"E1")])]})}),makeQuery(id+"F9.opSweep","SWEPT_FACE",FACE,{"disambiguationData":[OSD([sQuery(id+"F6.wireOp",EDGE,"E16"),sQuery(id+"F8.wireOp",EDGE,"E59")])]})]});
            var Q90;
            Q90=makeQuery(id+"F9.boolean.opBoolean","INTERSECT",EDGE,{"disambiguationData":[OD(0.0)],"derivedFrom":[makeQuery(id+"F3.boolean.opBoolean","SPLIT",FACE,{"disambiguationData":[OD(0.0)],"derivedFrom":makeQuery(id+"F1.opExtrude","SWEPT_FACE",FACE,{"disambiguationData":[OSD([sQuery(id+"F0.wireOp",EDGE,"E1")])]})}),makeQuery(id+"F9.opSweep","SWEPT_FACE",FACE,{"disambiguationData":[OSD([sQuery(id+"F6.wireOp",EDGE,"E15"),sQuery(id+"F8.wireOp",EDGE,"E59")])]})]});
            var Q91;
            Q91=makeQuery(id+"F9.boolean.opBoolean","INTERSECT",EDGE,{"disambiguationData":[OD(0.0)],"derivedFrom":[makeQuery(id+"F3.boolean.opBoolean","SPLIT",FACE,{"disambiguationData":[OD(0.0)],"derivedFrom":makeQuery(id+"F1.opExtrude","SWEPT_FACE",FACE,{"disambiguationData":[OSD([sQuery(id+"F0.wireOp",EDGE,"E1")])]})}),makeQuery(id+"F9.opSweep","SWEPT_FACE",FACE,{"disambiguationData":[OSD([sQuery(id+"F6.wireOp",EDGE,"E14"),sQuery(id+"F8.wireOp",EDGE,"E59")])]})]});
            var Q92;
            Q92=makeQuery(id+"F9.boolean.opBoolean","INTERSECT",EDGE,{"disambiguationData":[OD(0.0)],"derivedFrom":[makeQuery(id+"F3.boolean.opBoolean","SPLIT",FACE,{"disambiguationData":[OD(0.0)],"derivedFrom":makeQuery(id+"F1.opExtrude","SWEPT_FACE",FACE,{"disambiguationData":[OSD([sQuery(id+"F0.wireOp",EDGE,"E1")])]})}),makeQuery(id+"F9.opSweep","SWEPT_FACE",FACE,{"disambiguationData":[OSD([sQuery(id+"F6.wireOp",EDGE,"E13"),sQuery(id+"F8.wireOp",EDGE,"E59")])]})]});
            var Q93;
            Q93=makeQuery(id+"F9.boolean.opBoolean","INTERSECT",EDGE,{"disambiguationData":[OD(0.0)],"derivedFrom":[makeQuery(id+"F3.boolean.opBoolean","SPLIT",FACE,{"disambiguationData":[OD(0.0)],"derivedFrom":makeQuery(id+"F1.opExtrude","SWEPT_FACE",FACE,{"disambiguationData":[OSD([sQuery(id+"F0.wireOp",EDGE,"E1")])]})}),makeQuery(id+"F9.opSweep","SWEPT_FACE",FACE,{"disambiguationData":[OSD([sQuery(id+"F6.wireOp",EDGE,"E12"),sQuery(id+"F8.wireOp",EDGE,"E59")])]})]});
            var Q94;
            Q94=makeQuery(id+"F9.boolean.opBoolean","INTERSECT",EDGE,{"disambiguationData":[OD(0.0)],"derivedFrom":[makeQuery(id+"F3.boolean.opBoolean","SPLIT",FACE,{"disambiguationData":[OD(0.0)],"derivedFrom":makeQuery(id+"F1.opExtrude","SWEPT_FACE",FACE,{"disambiguationData":[OSD([sQuery(id+"F0.wireOp",EDGE,"E1")])]})}),makeQuery(id+"F9.opSweep","SWEPT_FACE",FACE,{"disambiguationData":[OSD([sQuery(id+"F6.wireOp",EDGE,"E11"),sQuery(id+"F8.wireOp",EDGE,"E59")])]})]});
            var Q95;
            Q95=makeQuery(id+"F9.boolean.opBoolean","INTERSECT",EDGE,{"disambiguationData":[OD(0.0)],"derivedFrom":[makeQuery(id+"F3.boolean.opBoolean","SPLIT",FACE,{"disambiguationData":[OD(0.0)],"derivedFrom":makeQuery(id+"F1.opExtrude","SWEPT_FACE",FACE,{"disambiguationData":[OSD([sQuery(id+"F0.wireOp",EDGE,"E1")])]})}),makeQuery(id+"F9.opSweep","SWEPT_FACE",FACE,{"disambiguationData":[OSD([sQuery(id+"F6.wireOp",EDGE,"E10"),sQuery(id+"F8.wireOp",EDGE,"E59")])]})]});
            var Q96;
            Q96=makeQuery(id+"F9.boolean.opBoolean","INTERSECT",EDGE,{"disambiguationData":[OD(0.0)],"derivedFrom":[makeQuery(id+"F3.boolean.opBoolean","SPLIT",FACE,{"disambiguationData":[OD(0.0)],"derivedFrom":makeQuery(id+"F1.opExtrude","SWEPT_FACE",FACE,{"disambiguationData":[OSD([sQuery(id+"F0.wireOp",EDGE,"E1")])]})}),makeQuery(id+"F9.opSweep","SWEPT_FACE",FACE,{"disambiguationData":[OSD([sQuery(id+"F6.wireOp",EDGE,"E9"),sQuery(id+"F8.wireOp",EDGE,"E59")])]})]});
            var Q97;
            Q97=makeQuery(id+"F9.boolean.opBoolean","INTERSECT",EDGE,{"disambiguationData":[OD(0.0)],"derivedFrom":[makeQuery(id+"F3.boolean.opBoolean","SPLIT",FACE,{"disambiguationData":[OD(0.0)],"derivedFrom":makeQuery(id+"F1.opExtrude","SWEPT_FACE",FACE,{"disambiguationData":[OSD([sQuery(id+"F0.wireOp",EDGE,"E1")])]})}),makeQuery(id+"F9.opSweep","SWEPT_FACE",FACE,{"disambiguationData":[OSD([sQuery(id+"F6.wireOp",EDGE,"E57"),sQuery(id+"F8.wireOp",EDGE,"E59")])]})]});
            fillet(context, id + "F10", {"entities" : qUnion([Q0, Q1, Q2, Q3, Q4, Q5, Q6, Q7, Q8, Q9, Q10, Q11, Q12, Q13, Q14, Q15, Q16, Q17, Q18, Q19, Q20, Q21, Q22, Q23, Q24, Q25, Q26, Q27, Q28, Q29, Q30, Q31, Q32, Q33, Q34, Q35, Q36, Q37, Q38, Q39, Q40, Q41, Q42, Q43, Q44, Q45, Q46, Q47, Q48, Q49, Q50, Q51, Q52, Q53, Q54, Q55, Q56, Q57, Q58, Q59, Q60, Q61, Q62, Q63, Q64, Q65, Q66, Q67, Q68, Q69, Q70, Q71, Q72, Q73, Q74, Q75, Q76, Q77, Q78, Q79, Q80, Q81, Q82, Q83, Q84, Q85, Q86, Q87, Q88, Q89, Q90, Q91, Q92, Q93, Q94, Q95, Q96, Q97]), "radius" : 2 * mm, "tangentPropagation" : true, "allowEdgeOverflow" : false});
        }
        {
            var Q0;
            Q0=qCreatedBy(makeId("Top.planeOp"),FACE);
            var sketch = newSketch(context, id + "F11", { "sketchPlane" : qUnion([Q0])});
            skCircle(sketch, "E60", {"center": v(0, -74.22) * mm, "radius": 6.6 * mm});
            skLineSegment(sketch, "E61", {"start": v(0, 35.86) * mm, "end": v(-10.52, 60.65) * mm});
            skLineSegment(sketch, "E62", {"start": v(-10.52, 60.65) * mm, "end": v(-1.37, 67.87) * mm});
            skLineSegment(sketch, "E63", {"start": v(-1.37, 67.87) * mm, "end": v(-14.67, 73.05) * mm});
            skLineSegment(sketch, "E64", {"start": v(-14.67, 73.05) * mm, "end": v(0, 84.24) * mm});
            skLineSegment(sketch, "E65.MirrorCS", {"start": v(0, 35.86) * mm, "end": v(10.52, 60.65) * mm});
            skLineSegment(sketch, "E66.MirrorCS", {"start": v(10.52, 60.65) * mm, "end": v(1.37, 67.87) * mm});
            skLineSegment(sketch, "E67.MirrorCS", {"start": v(1.37, 67.87) * mm, "end": v(14.67, 73.05) * mm});
            skLineSegment(sketch, "E68.MirrorCS", {"start": v(14.67, 73.05) * mm, "end": v(0, 84.24) * mm});
            skSolve(sketch);
        }
        {
            var Q0;
            Q0=makeQuery(id+"F11.imprint","IMPRINT",FACE,{"disambiguationData":[TD([[makeQuery(id+"F11.imprint","IMPRINT",EDGE,{"derivedFrom":sQuery(id+"F11.wireOp",EDGE,"E60")}),1.0]])]});
            extrude(context, id + "F12", {"entities" : qUnion([Q0]), "operationType" : NewBodyOperationType.REMOVE, "depth" : 6.1 * mm, "offsetDistance" : 25.4 * mm});
        }
        {
            var Q0;
            Q0=makeQuery(id+"F11.imprint","IMPRINT",FACE,{"disambiguationData":[TD([[makeQuery(id+"F11.imprint","IMPRINT",EDGE,{"derivedFrom":sQuery(id+"F11.wireOp",EDGE,"E61")}),-1.0]])]});
            extrude(context, id + "F13", {"entities" : qUnion([Q0]), "operationType" : NewBodyOperationType.REMOVE, "depth" : 9.14 * mm, "offsetDistance" : 25.4 * mm});
        }
    });
